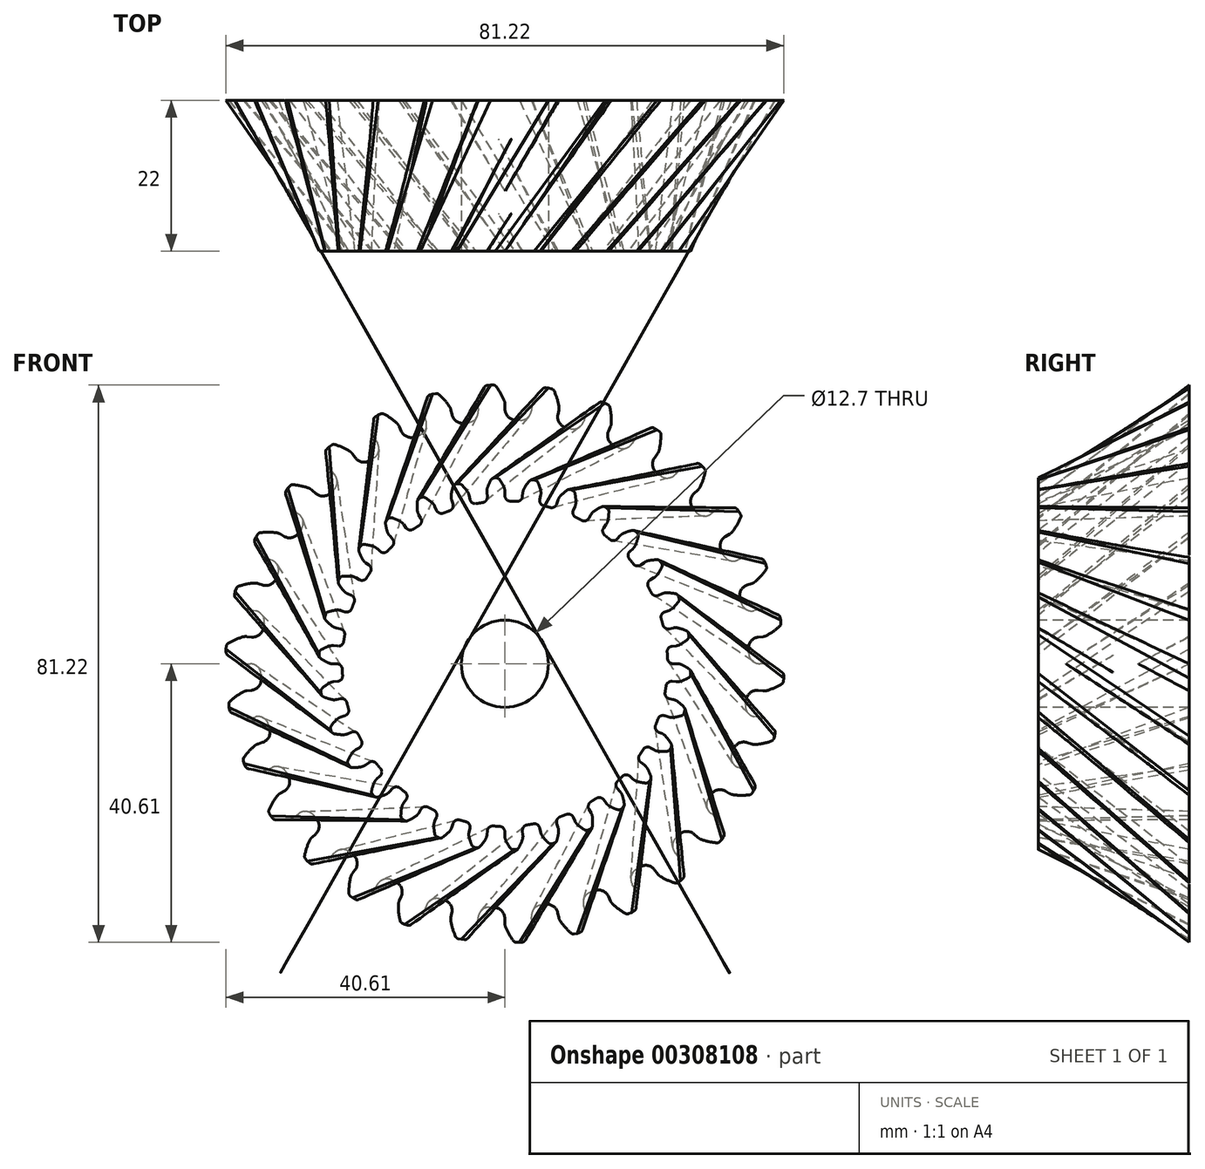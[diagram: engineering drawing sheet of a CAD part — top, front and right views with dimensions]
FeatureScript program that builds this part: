
annotation { "Feature Type Name" : "Feature", "Feature Type Description" : "" }
export const myFeature = defineFeature(function(context is Context, id is Id, definition is map)
    precondition{}
    {
        {
            var Q0;
            Q0=qCreatedBy(makeId("Front.planeOp"),FACE);
            var sketch = newSketch(context, id + "F0", { "sketchPlane" : qUnion([Q0])});
            skArc(sketch, "E0", {"start": v(-5.23, 35.17) * mm, "mid": v(-5.56, 35.12) * mm, "end": v(-5.9, 35.07) * mm});
            skArc(sketch, "E1.trimOffspring", {"start": v(-0.12, 38.41) * mm, "mid": v(-0.63, 39.45) * mm, "end": v(-1.27, 40.41) * mm});
            skLineSegment(sketch, "E2", {"start": v(-1.68, 40.61) * mm, "end": v(-2.13, 40.61) * mm});
            skLineSegment(sketch, "E3", {"start": v(0, 37.8) * mm, "end": v(0, 37.11) * mm});
            skLineSegment(sketch, "E4.MirrorCS", {"start": v(-2.58, 40.57) * mm, "end": v(-2.13, 40.61) * mm});
            skArc(sketch, "E5.MirrorCS", {"start": v(-3.9, 38.22) * mm, "mid": v(-3.5, 39.3) * mm, "end": v(-2.96, 40.32) * mm});
            skLineSegment(sketch, "E6.MirrorCS", {"start": v(-3.96, 37.58) * mm, "end": v(-3.89, 36.9) * mm});
            skPoint(sketch, "E7.visualSharp", {"position": v(-2.82, 40.54) * mm});
            skArc(sketch, "E7.filletArc", {"start": v(-2.58, 40.57) * mm, "mid": v(-2.8, 40.5) * mm, "end": v(-2.96, 40.32) * mm});
            skPoint(sketch, "E8.visualSharp", {"position": v(-1.43, 40.61) * mm});
            skArc(sketch, "E8.filletArc", {"start": v(-1.27, 40.41) * mm, "mid": v(-1.45, 40.56) * mm, "end": v(-1.68, 40.61) * mm});
            skPoint(sketch, "E9.visualSharp", {"position": v(-4, 37.9) * mm});
            skArc(sketch, "E9.filletArc", {"start": v(-3.9, 38.22) * mm, "mid": v(-3.96, 37.9) * mm, "end": v(-3.96, 37.58) * mm});
            skPoint(sketch, "E10.visualSharp", {"position": v(0, 38.1) * mm});
            skArc(sketch, "E10.filletArc", {"start": v(0, 37.8) * mm, "mid": v(-0.02, 38.1) * mm, "end": v(-0.12, 38.41) * mm});
            skPoint(sketch, "E11.visualSharp", {"position": v(0, 35.56) * mm});
            skArc(sketch, "E11.filletArc", {"start": v(0, 37.11) * mm, "mid": v(0.45, 36.02) * mm, "end": v(1.53, 35.53) * mm});
            skPoint(sketch, "E12.visualSharp", {"position": v(-3.73, 35.36) * mm});
            skArc(sketch, "E12.filletArc", {"start": v(-5.23, 35.17) * mm, "mid": v(-4.21, 35.77) * mm, "end": v(-3.89, 36.9) * mm});
            skArc(sketch, "E13.1.0", {"start": v(-12.43, 33.32) * mm, "mid": v(-11.56, 34.11) * mm, "end": v(-11.48, 35.3) * mm});
            skLineSegment(sketch, "E13.1.1", {"start": v(-11.69, 35.94) * mm, "end": v(-11.48, 35.3) * mm});
            skArc(sketch, "E13.1.2", {"start": v(-11.76, 36.57) * mm, "mid": v(-11.75, 36.25) * mm, "end": v(-11.69, 35.94) * mm});
            skArc(sketch, "E13.1.3", {"start": v(-11.76, 36.57) * mm, "mid": v(-11.59, 37.71) * mm, "end": v(-11.28, 38.83) * mm});
            skArc(sketch, "E13.1.4", {"start": v(-10.95, 39.15) * mm, "mid": v(-11.15, 39.02) * mm, "end": v(-11.28, 38.83) * mm});
            skLineSegment(sketch, "E13.1.5", {"start": v(-10.95, 39.15) * mm, "end": v(-10.53, 39.28) * mm});
            skLineSegment(sketch, "E13.1.6", {"start": v(-10.09, 39.38) * mm, "end": v(-10.53, 39.28) * mm});
            skArc(sketch, "E13.1.7", {"start": v(-9.65, 39.26) * mm, "mid": v(-9.85, 39.37) * mm, "end": v(-10.09, 39.38) * mm});
            skArc(sketch, "E13.1.8", {"start": v(-7.85, 36.97) * mm, "mid": v(-7.95, 37.27) * mm, "end": v(-8.1, 37.55) * mm});
            skLineSegment(sketch, "E13.1.9", {"start": v(-7.85, 36.97) * mm, "end": v(-7.7, 36.3) * mm});
            skArc(sketch, "E13.1.10", {"start": v(-7.7, 36.3) * mm, "mid": v(-7.05, 35.32) * mm, "end": v(-5.9, 35.07) * mm});
            skArc(sketch, "E13.1.11", {"start": v(-8.1, 37.55) * mm, "mid": v(-8.82, 38.45) * mm, "end": v(-9.65, 39.26) * mm});
            skArc(sketch, "E13.2.0", {"start": v(-19.09, 30) * mm, "mid": v(-18.4, 30.97) * mm, "end": v(-18.56, 32.14) * mm});
            skLineSegment(sketch, "E13.2.1", {"start": v(-18.9, 32.72) * mm, "end": v(-18.56, 32.14) * mm});
            skArc(sketch, "E13.2.2", {"start": v(-19.1, 33.33) * mm, "mid": v(-19.03, 33.01) * mm, "end": v(-18.9, 32.72) * mm});
            skArc(sketch, "E13.2.3", {"start": v(-19.1, 33.33) * mm, "mid": v(-19.17, 34.48) * mm, "end": v(-19.1, 35.63) * mm});
            skArc(sketch, "E13.2.4", {"start": v(-18.85, 36.01) * mm, "mid": v(-19.02, 35.85) * mm, "end": v(-19.1, 35.63) * mm});
            skLineSegment(sketch, "E13.2.5", {"start": v(-18.85, 36.01) * mm, "end": v(-18.46, 36.24) * mm});
            skLineSegment(sketch, "E13.2.6", {"start": v(-18.05, 36.42) * mm, "end": v(-18.46, 36.24) * mm});
            skArc(sketch, "E13.2.7", {"start": v(-17.6, 36.4) * mm, "mid": v(-17.82, 36.46) * mm, "end": v(-18.05, 36.42) * mm});
            skArc(sketch, "E13.2.8", {"start": v(-15.36, 34.53) * mm, "mid": v(-15.52, 34.8) * mm, "end": v(-15.73, 35.04) * mm});
            skLineSegment(sketch, "E13.2.9", {"start": v(-15.36, 34.53) * mm, "end": v(-15.09, 33.9) * mm});
            skArc(sketch, "E13.2.10", {"start": v(-15.09, 33.9) * mm, "mid": v(-14.24, 33.08) * mm, "end": v(-13.05, 33.08) * mm});
            skArc(sketch, "E13.2.11", {"start": v(-15.73, 35.04) * mm, "mid": v(-16.62, 35.78) * mm, "end": v(-17.6, 36.4) * mm});
            skArc(sketch, "E13.3.0", {"start": v(-24.9, 25.38) * mm, "mid": v(-24.43, 26.46) * mm, "end": v(-24.84, 27.57) * mm});
            skLineSegment(sketch, "E13.3.1", {"start": v(-25.3, 28.08) * mm, "end": v(-24.84, 27.57) * mm});
            skArc(sketch, "E13.3.2", {"start": v(-25.62, 28.63) * mm, "mid": v(-25.48, 28.34) * mm, "end": v(-25.3, 28.08) * mm});
            skArc(sketch, "E13.3.3", {"start": v(-25.62, 28.63) * mm, "mid": v(-25.92, 29.74) * mm, "end": v(-26.1, 30.88) * mm});
            skArc(sketch, "E13.3.4", {"start": v(-25.93, 31.3) * mm, "mid": v(-26.06, 31.11) * mm, "end": v(-26.1, 30.88) * mm});
            skLineSegment(sketch, "E13.3.5", {"start": v(-25.93, 31.3) * mm, "end": v(-25.6, 31.6) * mm});
            skLineSegment(sketch, "E13.3.6", {"start": v(-25.23, 31.87) * mm, "end": v(-25.6, 31.6) * mm});
            skArc(sketch, "E13.3.7", {"start": v(-24.78, 31.95) * mm, "mid": v(-25.02, 31.96) * mm, "end": v(-25.23, 31.87) * mm});
            skArc(sketch, "E13.3.8", {"start": v(-22.2, 30.58) * mm, "mid": v(-22.42, 30.82) * mm, "end": v(-22.67, 31) * mm});
            skLineSegment(sketch, "E13.3.9", {"start": v(-22.2, 30.58) * mm, "end": v(-21.8, 30.03) * mm});
            skArc(sketch, "E13.3.10", {"start": v(-21.8, 30.03) * mm, "mid": v(-20.8, 29.4) * mm, "end": v(-19.65, 29.64) * mm});
            skArc(sketch, "E13.3.11", {"start": v(-22.67, 31) * mm, "mid": v(-23.7, 31.54) * mm, "end": v(-24.78, 31.95) * mm});
            skArc(sketch, "E13.4.0", {"start": v(-29.64, 19.65) * mm, "mid": v(-29.4, 20.8) * mm, "end": v(-30.03, 21.8) * mm});
            skLineSegment(sketch, "E13.4.1", {"start": v(-30.58, 22.2) * mm, "end": v(-30.03, 21.8) * mm});
            skArc(sketch, "E13.4.2", {"start": v(-31, 22.67) * mm, "mid": v(-30.82, 22.42) * mm, "end": v(-30.58, 22.2) * mm});
            skArc(sketch, "E13.4.3", {"start": v(-31, 22.67) * mm, "mid": v(-31.54, 23.7) * mm, "end": v(-31.95, 24.78) * mm});
            skArc(sketch, "E13.4.4", {"start": v(-31.87, 25.23) * mm, "mid": v(-31.96, 25.02) * mm, "end": v(-31.95, 24.78) * mm});
            skLineSegment(sketch, "E13.4.5", {"start": v(-31.87, 25.23) * mm, "end": v(-31.6, 25.6) * mm});
            skLineSegment(sketch, "E13.4.6", {"start": v(-31.3, 25.93) * mm, "end": v(-31.6, 25.6) * mm});
            skArc(sketch, "E13.4.7", {"start": v(-30.88, 26.1) * mm, "mid": v(-31.11, 26.06) * mm, "end": v(-31.3, 25.93) * mm});
            skArc(sketch, "E13.4.8", {"start": v(-28.08, 25.3) * mm, "mid": v(-28.34, 25.48) * mm, "end": v(-28.63, 25.62) * mm});
            skLineSegment(sketch, "E13.4.9", {"start": v(-28.08, 25.3) * mm, "end": v(-27.57, 24.84) * mm});
            skArc(sketch, "E13.4.10", {"start": v(-27.57, 24.84) * mm, "mid": v(-26.46, 24.43) * mm, "end": v(-25.38, 24.9) * mm});
            skArc(sketch, "E13.4.11", {"start": v(-28.63, 25.62) * mm, "mid": v(-29.74, 25.92) * mm, "end": v(-30.88, 26.1) * mm});
            skArc(sketch, "E13.5.0", {"start": v(-33.08, 13.05) * mm, "mid": v(-33.08, 14.24) * mm, "end": v(-33.9, 15.09) * mm});
            skLineSegment(sketch, "E13.5.1", {"start": v(-34.53, 15.36) * mm, "end": v(-33.9, 15.09) * mm});
            skArc(sketch, "E13.5.2", {"start": v(-35.04, 15.73) * mm, "mid": v(-34.8, 15.52) * mm, "end": v(-34.53, 15.36) * mm});
            skArc(sketch, "E13.5.3", {"start": v(-35.04, 15.73) * mm, "mid": v(-35.78, 16.62) * mm, "end": v(-36.4, 17.6) * mm});
            skArc(sketch, "E13.5.4", {"start": v(-36.42, 18.05) * mm, "mid": v(-36.46, 17.82) * mm, "end": v(-36.4, 17.6) * mm});
            skLineSegment(sketch, "E13.5.5", {"start": v(-36.42, 18.05) * mm, "end": v(-36.24, 18.46) * mm});
            skLineSegment(sketch, "E13.5.6", {"start": v(-36.01, 18.85) * mm, "end": v(-36.24, 18.46) * mm});
            skArc(sketch, "E13.5.7", {"start": v(-35.63, 19.1) * mm, "mid": v(-35.85, 19.02) * mm, "end": v(-36.01, 18.85) * mm});
            skArc(sketch, "E13.5.8", {"start": v(-32.72, 18.9) * mm, "mid": v(-33.01, 19.03) * mm, "end": v(-33.33, 19.1) * mm});
            skLineSegment(sketch, "E13.5.9", {"start": v(-32.72, 18.9) * mm, "end": v(-32.14, 18.56) * mm});
            skArc(sketch, "E13.5.10", {"start": v(-32.14, 18.56) * mm, "mid": v(-30.97, 18.4) * mm, "end": v(-30, 19.09) * mm});
            skArc(sketch, "E13.5.11", {"start": v(-33.33, 19.1) * mm, "mid": v(-34.48, 19.17) * mm, "end": v(-35.63, 19.1) * mm});
            skArc(sketch, "E13.6.0", {"start": v(-35.07, 5.9) * mm, "mid": v(-35.32, 7.05) * mm, "end": v(-36.3, 7.7) * mm});
            skLineSegment(sketch, "E13.6.1", {"start": v(-36.97, 7.85) * mm, "end": v(-36.3, 7.7) * mm});
            skArc(sketch, "E13.6.2", {"start": v(-37.55, 8.1) * mm, "mid": v(-37.27, 7.95) * mm, "end": v(-36.97, 7.85) * mm});
            skArc(sketch, "E13.6.3", {"start": v(-37.55, 8.1) * mm, "mid": v(-38.45, 8.82) * mm, "end": v(-39.26, 9.65) * mm});
            skArc(sketch, "E13.6.4", {"start": v(-39.38, 10.09) * mm, "mid": v(-39.37, 9.85) * mm, "end": v(-39.26, 9.65) * mm});
            skLineSegment(sketch, "E13.6.5", {"start": v(-39.38, 10.09) * mm, "end": v(-39.28, 10.53) * mm});
            skLineSegment(sketch, "E13.6.6", {"start": v(-39.15, 10.95) * mm, "end": v(-39.28, 10.53) * mm});
            skArc(sketch, "E13.6.7", {"start": v(-38.83, 11.28) * mm, "mid": v(-39.02, 11.15) * mm, "end": v(-39.15, 10.95) * mm});
            skArc(sketch, "E13.6.8", {"start": v(-35.94, 11.69) * mm, "mid": v(-36.25, 11.75) * mm, "end": v(-36.57, 11.76) * mm});
            skLineSegment(sketch, "E13.6.9", {"start": v(-35.94, 11.69) * mm, "end": v(-35.3, 11.48) * mm});
            skArc(sketch, "E13.6.10", {"start": v(-35.3, 11.48) * mm, "mid": v(-34.11, 11.56) * mm, "end": v(-33.32, 12.43) * mm});
            skArc(sketch, "E13.6.11", {"start": v(-36.57, 11.76) * mm, "mid": v(-37.71, 11.59) * mm, "end": v(-38.83, 11.28) * mm});
            skArc(sketch, "E13.7.0", {"start": v(-35.53, -1.53) * mm, "mid": v(-36.02, -0.45) * mm, "end": v(-37.11, 0) * mm});
            skLineSegment(sketch, "E13.7.1", {"start": v(-37.8, 0) * mm, "end": v(-37.11, 0) * mm});
            skArc(sketch, "E13.7.2", {"start": v(-38.41, 0.12) * mm, "mid": v(-38.1, 0.02) * mm, "end": v(-37.8, 0) * mm});
            skArc(sketch, "E13.7.3", {"start": v(-38.41, 0.12) * mm, "mid": v(-39.45, 0.63) * mm, "end": v(-40.41, 1.27) * mm});
            skArc(sketch, "E13.7.4", {"start": v(-40.61, 1.68) * mm, "mid": v(-40.56, 1.45) * mm, "end": v(-40.41, 1.27) * mm});
            skLineSegment(sketch, "E13.7.5", {"start": v(-40.61, 1.68) * mm, "end": v(-40.61, 2.13) * mm});
            skLineSegment(sketch, "E13.7.6", {"start": v(-40.57, 2.58) * mm, "end": v(-40.61, 2.13) * mm});
            skArc(sketch, "E13.7.7", {"start": v(-40.32, 2.96) * mm, "mid": v(-40.5, 2.8) * mm, "end": v(-40.57, 2.58) * mm});
            skArc(sketch, "E13.7.8", {"start": v(-37.58, 3.96) * mm, "mid": v(-37.9, 3.96) * mm, "end": v(-38.22, 3.9) * mm});
            skLineSegment(sketch, "E13.7.9", {"start": v(-37.58, 3.96) * mm, "end": v(-36.9, 3.89) * mm});
            skArc(sketch, "E13.7.10", {"start": v(-36.9, 3.89) * mm, "mid": v(-35.77, 4.21) * mm, "end": v(-35.17, 5.23) * mm});
            skArc(sketch, "E13.7.11", {"start": v(-38.22, 3.9) * mm, "mid": v(-39.3, 3.5) * mm, "end": v(-40.32, 2.96) * mm});
            skArc(sketch, "E13.8.0", {"start": v(-34.43, -8.88) * mm, "mid": v(-35.13, -7.93) * mm, "end": v(-36.3, -7.72) * mm});
            skLineSegment(sketch, "E13.8.1", {"start": v(-36.96, -7.87) * mm, "end": v(-36.3, -7.72) * mm});
            skArc(sketch, "E13.8.2", {"start": v(-37.6, -7.87) * mm, "mid": v(-37.28, -7.9) * mm, "end": v(-36.96, -7.87) * mm});
            skArc(sketch, "E13.8.3", {"start": v(-37.6, -7.87) * mm, "mid": v(-38.72, -7.58) * mm, "end": v(-39.8, -7.16) * mm});
            skArc(sketch, "E13.8.4", {"start": v(-40.08, -6.8) * mm, "mid": v(-39.98, -7.01) * mm, "end": v(-39.8, -7.16) * mm});
            skLineSegment(sketch, "E13.8.5", {"start": v(-40.08, -6.8) * mm, "end": v(-40.17, -6.36) * mm});
            skLineSegment(sketch, "E13.8.6", {"start": v(-40.22, -5.92) * mm, "end": v(-40.17, -6.36) * mm});
            skArc(sketch, "E13.8.7", {"start": v(-40.06, -5.5) * mm, "mid": v(-40.19, -5.68) * mm, "end": v(-40.22, -5.92) * mm});
            skArc(sketch, "E13.8.8", {"start": v(-37.59, -3.94) * mm, "mid": v(-37.9, -4) * mm, "end": v(-38.2, -4.13) * mm});
            skLineSegment(sketch, "E13.8.9", {"start": v(-37.59, -3.94) * mm, "end": v(-36.91, -3.87) * mm});
            skArc(sketch, "E13.8.10", {"start": v(-36.91, -3.87) * mm, "mid": v(-35.86, -3.32) * mm, "end": v(-35.5, -2.2) * mm});
            skArc(sketch, "E13.8.11", {"start": v(-38.2, -4.13) * mm, "mid": v(-39.17, -4.75) * mm, "end": v(-40.06, -5.5) * mm});
            skArc(sketch, "E13.9.0", {"start": v(-31.83, -15.85) * mm, "mid": v(-32.72, -15.06) * mm, "end": v(-33.9, -15.1) * mm});
            skLineSegment(sketch, "E13.9.1", {"start": v(-34.52, -15.38) * mm, "end": v(-33.9, -15.1) * mm});
            skArc(sketch, "E13.9.2", {"start": v(-35.14, -15.52) * mm, "mid": v(-34.82, -15.48) * mm, "end": v(-34.52, -15.38) * mm});
            skArc(sketch, "E13.9.3", {"start": v(-35.14, -15.52) * mm, "mid": v(-36.3, -15.46) * mm, "end": v(-37.44, -15.27) * mm});
            skArc(sketch, "E13.9.4", {"start": v(-37.79, -14.99) * mm, "mid": v(-37.65, -15.17) * mm, "end": v(-37.44, -15.27) * mm});
            skLineSegment(sketch, "E13.9.5", {"start": v(-37.79, -14.99) * mm, "end": v(-37.97, -14.58) * mm});
            skLineSegment(sketch, "E13.9.6", {"start": v(-38.1, -14.15) * mm, "end": v(-37.97, -14.58) * mm});
            skArc(sketch, "E13.9.7", {"start": v(-38.04, -13.7) * mm, "mid": v(-38.13, -13.92) * mm, "end": v(-38.1, -14.15) * mm});
            skArc(sketch, "E13.9.8", {"start": v(-35.94, -11.67) * mm, "mid": v(-36.24, -11.8) * mm, "end": v(-36.5, -11.98) * mm});
            skLineSegment(sketch, "E13.9.9", {"start": v(-35.94, -11.67) * mm, "end": v(-35.3, -11.46) * mm});
            skArc(sketch, "E13.9.10", {"start": v(-35.3, -11.46) * mm, "mid": v(-34.4, -10.7) * mm, "end": v(-34.26, -9.53) * mm});
            skArc(sketch, "E13.9.11", {"start": v(-36.5, -11.98) * mm, "mid": v(-37.32, -12.8) * mm, "end": v(-38.04, -13.7) * mm});
            skArc(sketch, "E13.10.0", {"start": v(-27.84, -22.12) * mm, "mid": v(-28.87, -21.53) * mm, "end": v(-30.02, -21.82) * mm});
            skLineSegment(sketch, "E13.10.1", {"start": v(-30.57, -22.22) * mm, "end": v(-30.02, -21.82) * mm});
            skArc(sketch, "E13.10.2", {"start": v(-31.15, -22.48) * mm, "mid": v(-30.84, -22.38) * mm, "end": v(-30.57, -22.22) * mm});
            skArc(sketch, "E13.10.3", {"start": v(-31.15, -22.48) * mm, "mid": v(-32.29, -22.67) * mm, "end": v(-33.44, -22.72) * mm});
            skArc(sketch, "E13.10.4", {"start": v(-33.85, -22.51) * mm, "mid": v(-33.67, -22.67) * mm, "end": v(-33.44, -22.72) * mm});
            skLineSegment(sketch, "E13.10.5", {"start": v(-33.85, -22.51) * mm, "end": v(-34.1, -22.15) * mm});
            skLineSegment(sketch, "E13.10.6", {"start": v(-34.33, -21.76) * mm, "end": v(-34.1, -22.15) * mm});
            skArc(sketch, "E13.10.7", {"start": v(-34.36, -21.3) * mm, "mid": v(-34.4, -21.54) * mm, "end": v(-34.33, -21.76) * mm});
            skArc(sketch, "E13.10.8", {"start": v(-32.73, -18.89) * mm, "mid": v(-33, -19.07) * mm, "end": v(-33.2, -19.3) * mm});
            skLineSegment(sketch, "E13.10.9", {"start": v(-32.73, -18.89) * mm, "end": v(-32.15, -18.55) * mm});
            skArc(sketch, "E13.10.10", {"start": v(-32.15, -18.55) * mm, "mid": v(-31.41, -17.62) * mm, "end": v(-31.53, -16.44) * mm});
            skArc(sketch, "E13.10.11", {"start": v(-33.2, -19.3) * mm, "mid": v(-33.85, -20.27) * mm, "end": v(-34.36, -21.3) * mm});
            skArc(sketch, "E13.11.0", {"start": v(-22.64, -27.42) * mm, "mid": v(-23.76, -27.07) * mm, "end": v(-24.83, -27.59) * mm});
            skLineSegment(sketch, "E13.11.1", {"start": v(-25.28, -28.1) * mm, "end": v(-24.83, -27.59) * mm});
            skArc(sketch, "E13.11.2", {"start": v(-25.8, -28.47) * mm, "mid": v(-25.52, -28.3) * mm, "end": v(-25.28, -28.1) * mm});
            skArc(sketch, "E13.11.3", {"start": v(-25.8, -28.47) * mm, "mid": v(-26.87, -28.9) * mm, "end": v(-27.99, -29.18) * mm});
            skArc(sketch, "E13.11.4", {"start": v(-28.42, -29.06) * mm, "mid": v(-28.22, -29.17) * mm, "end": v(-27.99, -29.18) * mm});
            skLineSegment(sketch, "E13.11.5", {"start": v(-28.42, -29.06) * mm, "end": v(-28.76, -28.76) * mm});
            skLineSegment(sketch, "E13.11.6", {"start": v(-29.06, -28.42) * mm, "end": v(-28.76, -28.76) * mm});
            skArc(sketch, "E13.11.7", {"start": v(-29.18, -27.99) * mm, "mid": v(-29.17, -28.22) * mm, "end": v(-29.06, -28.42) * mm});
            skArc(sketch, "E13.11.8", {"start": v(-28.1, -25.28) * mm, "mid": v(-28.3, -25.52) * mm, "end": v(-28.47, -25.8) * mm});
            skLineSegment(sketch, "E13.11.9", {"start": v(-28.1, -25.28) * mm, "end": v(-27.59, -24.83) * mm});
            skArc(sketch, "E13.11.10", {"start": v(-27.59, -24.83) * mm, "mid": v(-27.07, -23.76) * mm, "end": v(-27.42, -22.64) * mm});
            skArc(sketch, "E13.11.11", {"start": v(-28.47, -25.8) * mm, "mid": v(-28.9, -26.87) * mm, "end": v(-29.18, -27.99) * mm});
            skArc(sketch, "E13.12.0", {"start": v(-16.44, -31.53) * mm, "mid": v(-17.62, -31.41) * mm, "end": v(-18.55, -32.15) * mm});
            skLineSegment(sketch, "E13.12.1", {"start": v(-18.89, -32.73) * mm, "end": v(-18.55, -32.15) * mm});
            skArc(sketch, "E13.12.2", {"start": v(-19.3, -33.2) * mm, "mid": v(-19.07, -33) * mm, "end": v(-18.89, -32.73) * mm});
            skArc(sketch, "E13.12.3", {"start": v(-19.3, -33.2) * mm, "mid": v(-20.27, -33.85) * mm, "end": v(-21.3, -34.36) * mm});
            skArc(sketch, "E13.12.4", {"start": v(-21.76, -34.33) * mm, "mid": v(-21.54, -34.4) * mm, "end": v(-21.3, -34.36) * mm});
            skLineSegment(sketch, "E13.12.5", {"start": v(-21.76, -34.33) * mm, "end": v(-22.15, -34.1) * mm});
            skLineSegment(sketch, "E13.12.6", {"start": v(-22.51, -33.85) * mm, "end": v(-22.15, -34.1) * mm});
            skArc(sketch, "E13.12.7", {"start": v(-22.72, -33.44) * mm, "mid": v(-22.67, -33.67) * mm, "end": v(-22.51, -33.85) * mm});
            skArc(sketch, "E13.12.8", {"start": v(-22.22, -30.57) * mm, "mid": v(-22.38, -30.84) * mm, "end": v(-22.48, -31.15) * mm});
            skLineSegment(sketch, "E13.12.9", {"start": v(-22.22, -30.57) * mm, "end": v(-21.82, -30.02) * mm});
            skArc(sketch, "E13.12.10", {"start": v(-21.82, -30.02) * mm, "mid": v(-21.53, -28.87) * mm, "end": v(-22.12, -27.84) * mm});
            skArc(sketch, "E13.12.11", {"start": v(-22.48, -31.15) * mm, "mid": v(-22.67, -32.29) * mm, "end": v(-22.72, -33.44) * mm});
            skArc(sketch, "E13.13.0", {"start": v(-9.53, -34.26) * mm, "mid": v(-10.7, -34.4) * mm, "end": v(-11.46, -35.3) * mm});
            skLineSegment(sketch, "E13.13.1", {"start": v(-11.67, -35.94) * mm, "end": v(-11.46, -35.3) * mm});
            skArc(sketch, "E13.13.2", {"start": v(-11.98, -36.5) * mm, "mid": v(-11.8, -36.24) * mm, "end": v(-11.67, -35.94) * mm});
            skArc(sketch, "E13.13.3", {"start": v(-11.98, -36.5) * mm, "mid": v(-12.8, -37.32) * mm, "end": v(-13.7, -38.04) * mm});
            skArc(sketch, "E13.13.4", {"start": v(-14.15, -38.1) * mm, "mid": v(-13.92, -38.13) * mm, "end": v(-13.7, -38.04) * mm});
            skLineSegment(sketch, "E13.13.5", {"start": v(-14.15, -38.1) * mm, "end": v(-14.58, -37.97) * mm});
            skLineSegment(sketch, "E13.13.6", {"start": v(-14.99, -37.79) * mm, "end": v(-14.58, -37.97) * mm});
            skArc(sketch, "E13.13.7", {"start": v(-15.27, -37.44) * mm, "mid": v(-15.17, -37.65) * mm, "end": v(-14.99, -37.79) * mm});
            skArc(sketch, "E13.13.8", {"start": v(-15.38, -34.52) * mm, "mid": v(-15.48, -34.82) * mm, "end": v(-15.52, -35.14) * mm});
            skLineSegment(sketch, "E13.13.9", {"start": v(-15.38, -34.52) * mm, "end": v(-15.1, -33.9) * mm});
            skArc(sketch, "E13.13.10", {"start": v(-15.1, -33.9) * mm, "mid": v(-15.06, -32.72) * mm, "end": v(-15.85, -31.83) * mm});
            skArc(sketch, "E13.13.11", {"start": v(-15.52, -35.14) * mm, "mid": v(-15.46, -36.3) * mm, "end": v(-15.27, -37.44) * mm});
            skArc(sketch, "E13.14.0", {"start": v(-2.2, -35.5) * mm, "mid": v(-3.32, -35.86) * mm, "end": v(-3.87, -36.91) * mm});
            skLineSegment(sketch, "E13.14.1", {"start": v(-3.94, -37.59) * mm, "end": v(-3.87, -36.91) * mm});
            skArc(sketch, "E13.14.2", {"start": v(-4.13, -38.2) * mm, "mid": v(-4, -37.9) * mm, "end": v(-3.94, -37.59) * mm});
            skArc(sketch, "E13.14.3", {"start": v(-4.13, -38.2) * mm, "mid": v(-4.75, -39.17) * mm, "end": v(-5.5, -40.06) * mm});
            skArc(sketch, "E13.14.4", {"start": v(-5.92, -40.22) * mm, "mid": v(-5.68, -40.19) * mm, "end": v(-5.5, -40.06) * mm});
            skLineSegment(sketch, "E13.14.5", {"start": v(-5.92, -40.22) * mm, "end": v(-6.36, -40.17) * mm});
            skLineSegment(sketch, "E13.14.6", {"start": v(-6.8, -40.08) * mm, "end": v(-6.36, -40.17) * mm});
            skArc(sketch, "E13.14.7", {"start": v(-7.16, -39.8) * mm, "mid": v(-7.01, -39.98) * mm, "end": v(-6.8, -40.08) * mm});
            skArc(sketch, "E13.14.8", {"start": v(-7.87, -36.96) * mm, "mid": v(-7.9, -37.28) * mm, "end": v(-7.87, -37.6) * mm});
            skLineSegment(sketch, "E13.14.9", {"start": v(-7.87, -36.96) * mm, "end": v(-7.72, -36.3) * mm});
            skArc(sketch, "E13.14.10", {"start": v(-7.72, -36.3) * mm, "mid": v(-7.93, -35.13) * mm, "end": v(-8.88, -34.43) * mm});
            skArc(sketch, "E13.14.11", {"start": v(-7.87, -37.6) * mm, "mid": v(-7.58, -38.72) * mm, "end": v(-7.16, -39.8) * mm});
            skArc(sketch, "E13.15.0", {"start": v(5.23, -35.17) * mm, "mid": v(4.21, -35.77) * mm, "end": v(3.89, -36.9) * mm});
            skLineSegment(sketch, "E13.15.1", {"start": v(3.96, -37.58) * mm, "end": v(3.89, -36.9) * mm});
            skArc(sketch, "E13.15.2", {"start": v(3.9, -38.22) * mm, "mid": v(3.96, -37.9) * mm, "end": v(3.96, -37.58) * mm});
            skArc(sketch, "E13.15.3", {"start": v(3.9, -38.22) * mm, "mid": v(3.5, -39.3) * mm, "end": v(2.96, -40.32) * mm});
            skArc(sketch, "E13.15.4", {"start": v(2.58, -40.57) * mm, "mid": v(2.8, -40.5) * mm, "end": v(2.96, -40.32) * mm});
            skLineSegment(sketch, "E13.15.5", {"start": v(2.58, -40.57) * mm, "end": v(2.13, -40.61) * mm});
            skLineSegment(sketch, "E13.15.6", {"start": v(1.68, -40.61) * mm, "end": v(2.13, -40.61) * mm});
            skArc(sketch, "E13.15.7", {"start": v(1.27, -40.41) * mm, "mid": v(1.45, -40.56) * mm, "end": v(1.68, -40.61) * mm});
            skArc(sketch, "E13.15.8", {"start": v(0, -37.8) * mm, "mid": v(0.02, -38.1) * mm, "end": v(0.12, -38.41) * mm});
            skLineSegment(sketch, "E13.15.9", {"start": v(0, -37.8) * mm, "end": v(0, -37.11) * mm});
            skArc(sketch, "E13.15.10", {"start": v(0, -37.11) * mm, "mid": v(-0.45, -36.02) * mm, "end": v(-1.53, -35.53) * mm});
            skArc(sketch, "E13.15.11", {"start": v(0.12, -38.41) * mm, "mid": v(0.63, -39.45) * mm, "end": v(1.27, -40.41) * mm});
            skArc(sketch, "E13.16.0", {"start": v(12.43, -33.32) * mm, "mid": v(11.56, -34.11) * mm, "end": v(11.48, -35.3) * mm});
            skLineSegment(sketch, "E13.16.1", {"start": v(11.69, -35.94) * mm, "end": v(11.48, -35.3) * mm});
            skArc(sketch, "E13.16.2", {"start": v(11.76, -36.57) * mm, "mid": v(11.75, -36.25) * mm, "end": v(11.69, -35.94) * mm});
            skArc(sketch, "E13.16.3", {"start": v(11.76, -36.57) * mm, "mid": v(11.59, -37.71) * mm, "end": v(11.28, -38.83) * mm});
            skArc(sketch, "E13.16.4", {"start": v(10.95, -39.15) * mm, "mid": v(11.15, -39.02) * mm, "end": v(11.28, -38.83) * mm});
            skLineSegment(sketch, "E13.16.5", {"start": v(10.95, -39.15) * mm, "end": v(10.53, -39.28) * mm});
            skLineSegment(sketch, "E13.16.6", {"start": v(10.09, -39.38) * mm, "end": v(10.53, -39.28) * mm});
            skArc(sketch, "E13.16.7", {"start": v(9.65, -39.26) * mm, "mid": v(9.85, -39.37) * mm, "end": v(10.09, -39.38) * mm});
            skArc(sketch, "E13.16.8", {"start": v(7.85, -36.97) * mm, "mid": v(7.95, -37.27) * mm, "end": v(8.1, -37.55) * mm});
            skLineSegment(sketch, "E13.16.9", {"start": v(7.85, -36.97) * mm, "end": v(7.7, -36.3) * mm});
            skArc(sketch, "E13.16.10", {"start": v(7.7, -36.3) * mm, "mid": v(7.05, -35.32) * mm, "end": v(5.9, -35.07) * mm});
            skArc(sketch, "E13.16.11", {"start": v(8.1, -37.55) * mm, "mid": v(8.82, -38.45) * mm, "end": v(9.65, -39.26) * mm});
            skArc(sketch, "E13.17.0", {"start": v(19.09, -30) * mm, "mid": v(18.4, -30.97) * mm, "end": v(18.56, -32.14) * mm});
            skLineSegment(sketch, "E13.17.1", {"start": v(18.9, -32.72) * mm, "end": v(18.56, -32.14) * mm});
            skArc(sketch, "E13.17.2", {"start": v(19.1, -33.33) * mm, "mid": v(19.03, -33.01) * mm, "end": v(18.9, -32.72) * mm});
            skArc(sketch, "E13.17.3", {"start": v(19.1, -33.33) * mm, "mid": v(19.17, -34.48) * mm, "end": v(19.1, -35.63) * mm});
            skArc(sketch, "E13.17.4", {"start": v(18.85, -36.01) * mm, "mid": v(19.02, -35.85) * mm, "end": v(19.1, -35.63) * mm});
            skLineSegment(sketch, "E13.17.5", {"start": v(18.85, -36.01) * mm, "end": v(18.46, -36.24) * mm});
            skLineSegment(sketch, "E13.17.6", {"start": v(18.05, -36.42) * mm, "end": v(18.46, -36.24) * mm});
            skArc(sketch, "E13.17.7", {"start": v(17.6, -36.4) * mm, "mid": v(17.82, -36.46) * mm, "end": v(18.05, -36.42) * mm});
            skArc(sketch, "E13.17.8", {"start": v(15.36, -34.53) * mm, "mid": v(15.52, -34.8) * mm, "end": v(15.73, -35.04) * mm});
            skLineSegment(sketch, "E13.17.9", {"start": v(15.36, -34.53) * mm, "end": v(15.09, -33.9) * mm});
            skArc(sketch, "E13.17.10", {"start": v(15.09, -33.9) * mm, "mid": v(14.24, -33.08) * mm, "end": v(13.05, -33.08) * mm});
            skArc(sketch, "E13.17.11", {"start": v(15.73, -35.04) * mm, "mid": v(16.62, -35.78) * mm, "end": v(17.6, -36.4) * mm});
            skArc(sketch, "E13.18.0", {"start": v(24.9, -25.38) * mm, "mid": v(24.43, -26.46) * mm, "end": v(24.84, -27.57) * mm});
            skLineSegment(sketch, "E13.18.1", {"start": v(25.3, -28.08) * mm, "end": v(24.84, -27.57) * mm});
            skArc(sketch, "E13.18.2", {"start": v(25.62, -28.63) * mm, "mid": v(25.48, -28.34) * mm, "end": v(25.3, -28.08) * mm});
            skArc(sketch, "E13.18.3", {"start": v(25.62, -28.63) * mm, "mid": v(25.92, -29.74) * mm, "end": v(26.1, -30.88) * mm});
            skArc(sketch, "E13.18.4", {"start": v(25.93, -31.3) * mm, "mid": v(26.06, -31.11) * mm, "end": v(26.1, -30.88) * mm});
            skLineSegment(sketch, "E13.18.5", {"start": v(25.93, -31.3) * mm, "end": v(25.6, -31.6) * mm});
            skLineSegment(sketch, "E13.18.6", {"start": v(25.23, -31.87) * mm, "end": v(25.6, -31.6) * mm});
            skArc(sketch, "E13.18.7", {"start": v(24.78, -31.95) * mm, "mid": v(25.02, -31.96) * mm, "end": v(25.23, -31.87) * mm});
            skArc(sketch, "E13.18.8", {"start": v(22.2, -30.58) * mm, "mid": v(22.42, -30.82) * mm, "end": v(22.67, -31) * mm});
            skLineSegment(sketch, "E13.18.9", {"start": v(22.2, -30.58) * mm, "end": v(21.8, -30.03) * mm});
            skArc(sketch, "E13.18.10", {"start": v(21.8, -30.03) * mm, "mid": v(20.8, -29.4) * mm, "end": v(19.65, -29.64) * mm});
            skArc(sketch, "E13.18.11", {"start": v(22.67, -31) * mm, "mid": v(23.7, -31.54) * mm, "end": v(24.78, -31.95) * mm});
            skArc(sketch, "E13.19.0", {"start": v(29.64, -19.65) * mm, "mid": v(29.4, -20.8) * mm, "end": v(30.03, -21.8) * mm});
            skLineSegment(sketch, "E13.19.1", {"start": v(30.58, -22.2) * mm, "end": v(30.03, -21.8) * mm});
            skArc(sketch, "E13.19.2", {"start": v(31, -22.67) * mm, "mid": v(30.82, -22.42) * mm, "end": v(30.58, -22.2) * mm});
            skArc(sketch, "E13.19.3", {"start": v(31, -22.67) * mm, "mid": v(31.54, -23.7) * mm, "end": v(31.95, -24.78) * mm});
            skArc(sketch, "E13.19.4", {"start": v(31.87, -25.23) * mm, "mid": v(31.96, -25.02) * mm, "end": v(31.95, -24.78) * mm});
            skLineSegment(sketch, "E13.19.5", {"start": v(31.87, -25.23) * mm, "end": v(31.6, -25.6) * mm});
            skLineSegment(sketch, "E13.19.6", {"start": v(31.3, -25.93) * mm, "end": v(31.6, -25.6) * mm});
            skArc(sketch, "E13.19.7", {"start": v(30.88, -26.1) * mm, "mid": v(31.11, -26.06) * mm, "end": v(31.3, -25.93) * mm});
            skArc(sketch, "E13.19.8", {"start": v(28.08, -25.3) * mm, "mid": v(28.34, -25.48) * mm, "end": v(28.63, -25.62) * mm});
            skLineSegment(sketch, "E13.19.9", {"start": v(28.08, -25.3) * mm, "end": v(27.57, -24.84) * mm});
            skArc(sketch, "E13.19.10", {"start": v(27.57, -24.84) * mm, "mid": v(26.46, -24.43) * mm, "end": v(25.38, -24.9) * mm});
            skArc(sketch, "E13.19.11", {"start": v(28.63, -25.62) * mm, "mid": v(29.74, -25.92) * mm, "end": v(30.88, -26.1) * mm});
            skArc(sketch, "E13.20.0", {"start": v(33.08, -13.05) * mm, "mid": v(33.08, -14.24) * mm, "end": v(33.9, -15.09) * mm});
            skLineSegment(sketch, "E13.20.1", {"start": v(34.53, -15.36) * mm, "end": v(33.9, -15.09) * mm});
            skArc(sketch, "E13.20.2", {"start": v(35.04, -15.73) * mm, "mid": v(34.8, -15.52) * mm, "end": v(34.53, -15.36) * mm});
            skArc(sketch, "E13.20.3", {"start": v(35.04, -15.73) * mm, "mid": v(35.78, -16.62) * mm, "end": v(36.4, -17.6) * mm});
            skArc(sketch, "E13.20.4", {"start": v(36.42, -18.05) * mm, "mid": v(36.46, -17.82) * mm, "end": v(36.4, -17.6) * mm});
            skLineSegment(sketch, "E13.20.5", {"start": v(36.42, -18.05) * mm, "end": v(36.24, -18.46) * mm});
            skLineSegment(sketch, "E13.20.6", {"start": v(36.01, -18.85) * mm, "end": v(36.24, -18.46) * mm});
            skArc(sketch, "E13.20.7", {"start": v(35.63, -19.1) * mm, "mid": v(35.85, -19.02) * mm, "end": v(36.01, -18.85) * mm});
            skArc(sketch, "E13.20.8", {"start": v(32.72, -18.9) * mm, "mid": v(33.01, -19.03) * mm, "end": v(33.33, -19.1) * mm});
            skLineSegment(sketch, "E13.20.9", {"start": v(32.72, -18.9) * mm, "end": v(32.14, -18.56) * mm});
            skArc(sketch, "E13.20.10", {"start": v(32.14, -18.56) * mm, "mid": v(30.97, -18.4) * mm, "end": v(30, -19.09) * mm});
            skArc(sketch, "E13.20.11", {"start": v(33.33, -19.1) * mm, "mid": v(34.48, -19.17) * mm, "end": v(35.63, -19.1) * mm});
            skArc(sketch, "E13.21.0", {"start": v(35.07, -5.9) * mm, "mid": v(35.32, -7.05) * mm, "end": v(36.3, -7.7) * mm});
            skLineSegment(sketch, "E13.21.1", {"start": v(36.97, -7.85) * mm, "end": v(36.3, -7.7) * mm});
            skArc(sketch, "E13.21.2", {"start": v(37.55, -8.1) * mm, "mid": v(37.27, -7.95) * mm, "end": v(36.97, -7.85) * mm});
            skArc(sketch, "E13.21.3", {"start": v(37.55, -8.1) * mm, "mid": v(38.45, -8.82) * mm, "end": v(39.26, -9.65) * mm});
            skArc(sketch, "E13.21.4", {"start": v(39.38, -10.09) * mm, "mid": v(39.37, -9.85) * mm, "end": v(39.26, -9.65) * mm});
            skLineSegment(sketch, "E13.21.5", {"start": v(39.38, -10.09) * mm, "end": v(39.28, -10.53) * mm});
            skLineSegment(sketch, "E13.21.6", {"start": v(39.15, -10.95) * mm, "end": v(39.28, -10.53) * mm});
            skArc(sketch, "E13.21.7", {"start": v(38.83, -11.28) * mm, "mid": v(39.02, -11.15) * mm, "end": v(39.15, -10.95) * mm});
            skArc(sketch, "E13.21.8", {"start": v(35.94, -11.69) * mm, "mid": v(36.25, -11.75) * mm, "end": v(36.57, -11.76) * mm});
            skLineSegment(sketch, "E13.21.9", {"start": v(35.94, -11.69) * mm, "end": v(35.3, -11.48) * mm});
            skArc(sketch, "E13.21.10", {"start": v(35.3, -11.48) * mm, "mid": v(34.11, -11.56) * mm, "end": v(33.32, -12.43) * mm});
            skArc(sketch, "E13.21.11", {"start": v(36.57, -11.76) * mm, "mid": v(37.71, -11.59) * mm, "end": v(38.83, -11.28) * mm});
            skArc(sketch, "E13.22.0", {"start": v(35.53, 1.53) * mm, "mid": v(36.02, 0.45) * mm, "end": v(37.11, 0) * mm});
            skLineSegment(sketch, "E13.22.1", {"start": v(37.8, 0) * mm, "end": v(37.11, 0) * mm});
            skArc(sketch, "E13.22.2", {"start": v(38.41, -0.12) * mm, "mid": v(38.1, -0.02) * mm, "end": v(37.8, 0) * mm});
            skArc(sketch, "E13.22.3", {"start": v(38.41, -0.12) * mm, "mid": v(39.45, -0.63) * mm, "end": v(40.41, -1.27) * mm});
            skArc(sketch, "E13.22.4", {"start": v(40.61, -1.68) * mm, "mid": v(40.56, -1.45) * mm, "end": v(40.41, -1.27) * mm});
            skLineSegment(sketch, "E13.22.5", {"start": v(40.61, -1.68) * mm, "end": v(40.61, -2.13) * mm});
            skLineSegment(sketch, "E13.22.6", {"start": v(40.57, -2.58) * mm, "end": v(40.61, -2.13) * mm});
            skArc(sketch, "E13.22.7", {"start": v(40.32, -2.96) * mm, "mid": v(40.5, -2.8) * mm, "end": v(40.57, -2.58) * mm});
            skArc(sketch, "E13.22.8", {"start": v(37.58, -3.96) * mm, "mid": v(37.9, -3.96) * mm, "end": v(38.22, -3.9) * mm});
            skLineSegment(sketch, "E13.22.9", {"start": v(37.58, -3.96) * mm, "end": v(36.9, -3.89) * mm});
            skArc(sketch, "E13.22.10", {"start": v(36.9, -3.89) * mm, "mid": v(35.77, -4.21) * mm, "end": v(35.17, -5.23) * mm});
            skArc(sketch, "E13.22.11", {"start": v(38.22, -3.9) * mm, "mid": v(39.3, -3.5) * mm, "end": v(40.32, -2.96) * mm});
            skArc(sketch, "E13.23.0", {"start": v(34.43, 8.88) * mm, "mid": v(35.13, 7.93) * mm, "end": v(36.3, 7.72) * mm});
            skLineSegment(sketch, "E13.23.1", {"start": v(36.96, 7.87) * mm, "end": v(36.3, 7.72) * mm});
            skArc(sketch, "E13.23.2", {"start": v(37.6, 7.87) * mm, "mid": v(37.28, 7.9) * mm, "end": v(36.96, 7.87) * mm});
            skArc(sketch, "E13.23.3", {"start": v(37.6, 7.87) * mm, "mid": v(38.72, 7.58) * mm, "end": v(39.8, 7.16) * mm});
            skArc(sketch, "E13.23.4", {"start": v(40.08, 6.8) * mm, "mid": v(39.98, 7.01) * mm, "end": v(39.8, 7.16) * mm});
            skLineSegment(sketch, "E13.23.5", {"start": v(40.08, 6.8) * mm, "end": v(40.17, 6.36) * mm});
            skLineSegment(sketch, "E13.23.6", {"start": v(40.22, 5.92) * mm, "end": v(40.17, 6.36) * mm});
            skArc(sketch, "E13.23.7", {"start": v(40.06, 5.5) * mm, "mid": v(40.19, 5.68) * mm, "end": v(40.22, 5.92) * mm});
            skArc(sketch, "E13.23.8", {"start": v(37.59, 3.94) * mm, "mid": v(37.9, 4) * mm, "end": v(38.2, 4.13) * mm});
            skLineSegment(sketch, "E13.23.9", {"start": v(37.59, 3.94) * mm, "end": v(36.91, 3.87) * mm});
            skArc(sketch, "E13.23.10", {"start": v(36.91, 3.87) * mm, "mid": v(35.86, 3.32) * mm, "end": v(35.5, 2.2) * mm});
            skArc(sketch, "E13.23.11", {"start": v(38.2, 4.13) * mm, "mid": v(39.17, 4.75) * mm, "end": v(40.06, 5.5) * mm});
            skArc(sketch, "E13.24.0", {"start": v(31.83, 15.85) * mm, "mid": v(32.72, 15.06) * mm, "end": v(33.9, 15.1) * mm});
            skLineSegment(sketch, "E13.24.1", {"start": v(34.52, 15.38) * mm, "end": v(33.9, 15.1) * mm});
            skArc(sketch, "E13.24.2", {"start": v(35.14, 15.52) * mm, "mid": v(34.82, 15.48) * mm, "end": v(34.52, 15.38) * mm});
            skArc(sketch, "E13.24.3", {"start": v(35.14, 15.52) * mm, "mid": v(36.3, 15.46) * mm, "end": v(37.44, 15.27) * mm});
            skArc(sketch, "E13.24.4", {"start": v(37.79, 14.99) * mm, "mid": v(37.65, 15.17) * mm, "end": v(37.44, 15.27) * mm});
            skLineSegment(sketch, "E13.24.5", {"start": v(37.79, 14.99) * mm, "end": v(37.97, 14.58) * mm});
            skLineSegment(sketch, "E13.24.6", {"start": v(38.1, 14.15) * mm, "end": v(37.97, 14.58) * mm});
            skArc(sketch, "E13.24.7", {"start": v(38.04, 13.7) * mm, "mid": v(38.13, 13.92) * mm, "end": v(38.1, 14.15) * mm});
            skArc(sketch, "E13.24.8", {"start": v(35.94, 11.67) * mm, "mid": v(36.24, 11.8) * mm, "end": v(36.5, 11.98) * mm});
            skLineSegment(sketch, "E13.24.9", {"start": v(35.94, 11.67) * mm, "end": v(35.3, 11.46) * mm});
            skArc(sketch, "E13.24.10", {"start": v(35.3, 11.46) * mm, "mid": v(34.4, 10.7) * mm, "end": v(34.26, 9.53) * mm});
            skArc(sketch, "E13.24.11", {"start": v(36.5, 11.98) * mm, "mid": v(37.32, 12.8) * mm, "end": v(38.04, 13.7) * mm});
            skArc(sketch, "E13.25.0", {"start": v(27.84, 22.12) * mm, "mid": v(28.87, 21.53) * mm, "end": v(30.02, 21.82) * mm});
            skLineSegment(sketch, "E13.25.1", {"start": v(30.57, 22.22) * mm, "end": v(30.02, 21.82) * mm});
            skArc(sketch, "E13.25.2", {"start": v(31.15, 22.48) * mm, "mid": v(30.84, 22.38) * mm, "end": v(30.57, 22.22) * mm});
            skArc(sketch, "E13.25.3", {"start": v(31.15, 22.48) * mm, "mid": v(32.29, 22.67) * mm, "end": v(33.44, 22.72) * mm});
            skArc(sketch, "E13.25.4", {"start": v(33.85, 22.51) * mm, "mid": v(33.67, 22.67) * mm, "end": v(33.44, 22.72) * mm});
            skLineSegment(sketch, "E13.25.5", {"start": v(33.85, 22.51) * mm, "end": v(34.1, 22.15) * mm});
            skLineSegment(sketch, "E13.25.6", {"start": v(34.33, 21.76) * mm, "end": v(34.1, 22.15) * mm});
            skArc(sketch, "E13.25.7", {"start": v(34.36, 21.3) * mm, "mid": v(34.4, 21.54) * mm, "end": v(34.33, 21.76) * mm});
            skArc(sketch, "E13.25.8", {"start": v(32.73, 18.89) * mm, "mid": v(33, 19.07) * mm, "end": v(33.2, 19.3) * mm});
            skLineSegment(sketch, "E13.25.9", {"start": v(32.73, 18.89) * mm, "end": v(32.15, 18.55) * mm});
            skArc(sketch, "E13.25.10", {"start": v(32.15, 18.55) * mm, "mid": v(31.41, 17.62) * mm, "end": v(31.53, 16.44) * mm});
            skArc(sketch, "E13.25.11", {"start": v(33.2, 19.3) * mm, "mid": v(33.85, 20.27) * mm, "end": v(34.36, 21.3) * mm});
            skArc(sketch, "E13.26.0", {"start": v(22.64, 27.42) * mm, "mid": v(23.76, 27.07) * mm, "end": v(24.83, 27.59) * mm});
            skLineSegment(sketch, "E13.26.1", {"start": v(25.28, 28.1) * mm, "end": v(24.83, 27.59) * mm});
            skArc(sketch, "E13.26.2", {"start": v(25.8, 28.47) * mm, "mid": v(25.52, 28.3) * mm, "end": v(25.28, 28.1) * mm});
            skArc(sketch, "E13.26.3", {"start": v(25.8, 28.47) * mm, "mid": v(26.87, 28.9) * mm, "end": v(27.99, 29.18) * mm});
            skArc(sketch, "E13.26.4", {"start": v(28.42, 29.06) * mm, "mid": v(28.22, 29.17) * mm, "end": v(27.99, 29.18) * mm});
            skLineSegment(sketch, "E13.26.5", {"start": v(28.42, 29.06) * mm, "end": v(28.76, 28.76) * mm});
            skLineSegment(sketch, "E13.26.6", {"start": v(29.06, 28.42) * mm, "end": v(28.76, 28.76) * mm});
            skArc(sketch, "E13.26.7", {"start": v(29.18, 27.99) * mm, "mid": v(29.17, 28.22) * mm, "end": v(29.06, 28.42) * mm});
            skArc(sketch, "E13.26.8", {"start": v(28.1, 25.28) * mm, "mid": v(28.3, 25.52) * mm, "end": v(28.47, 25.8) * mm});
            skLineSegment(sketch, "E13.26.9", {"start": v(28.1, 25.28) * mm, "end": v(27.59, 24.83) * mm});
            skArc(sketch, "E13.26.10", {"start": v(27.59, 24.83) * mm, "mid": v(27.07, 23.76) * mm, "end": v(27.42, 22.64) * mm});
            skArc(sketch, "E13.26.11", {"start": v(28.47, 25.8) * mm, "mid": v(28.9, 26.87) * mm, "end": v(29.18, 27.99) * mm});
            skArc(sketch, "E13.27.0", {"start": v(16.44, 31.53) * mm, "mid": v(17.62, 31.41) * mm, "end": v(18.55, 32.15) * mm});
            skLineSegment(sketch, "E13.27.1", {"start": v(18.89, 32.73) * mm, "end": v(18.55, 32.15) * mm});
            skArc(sketch, "E13.27.2", {"start": v(19.3, 33.2) * mm, "mid": v(19.07, 33) * mm, "end": v(18.89, 32.73) * mm});
            skArc(sketch, "E13.27.3", {"start": v(19.3, 33.2) * mm, "mid": v(20.27, 33.85) * mm, "end": v(21.3, 34.36) * mm});
            skArc(sketch, "E13.27.4", {"start": v(21.76, 34.33) * mm, "mid": v(21.54, 34.4) * mm, "end": v(21.3, 34.36) * mm});
            skLineSegment(sketch, "E13.27.5", {"start": v(21.76, 34.33) * mm, "end": v(22.15, 34.1) * mm});
            skLineSegment(sketch, "E13.27.6", {"start": v(22.51, 33.85) * mm, "end": v(22.15, 34.1) * mm});
            skArc(sketch, "E13.27.7", {"start": v(22.72, 33.44) * mm, "mid": v(22.67, 33.67) * mm, "end": v(22.51, 33.85) * mm});
            skArc(sketch, "E13.27.8", {"start": v(22.22, 30.57) * mm, "mid": v(22.38, 30.84) * mm, "end": v(22.48, 31.15) * mm});
            skLineSegment(sketch, "E13.27.9", {"start": v(22.22, 30.57) * mm, "end": v(21.82, 30.02) * mm});
            skArc(sketch, "E13.27.10", {"start": v(21.82, 30.02) * mm, "mid": v(21.53, 28.87) * mm, "end": v(22.12, 27.84) * mm});
            skArc(sketch, "E13.27.11", {"start": v(22.48, 31.15) * mm, "mid": v(22.67, 32.29) * mm, "end": v(22.72, 33.44) * mm});
            skArc(sketch, "E13.28.0", {"start": v(9.53, 34.26) * mm, "mid": v(10.7, 34.4) * mm, "end": v(11.46, 35.3) * mm});
            skLineSegment(sketch, "E13.28.1", {"start": v(11.67, 35.94) * mm, "end": v(11.46, 35.3) * mm});
            skArc(sketch, "E13.28.2", {"start": v(11.98, 36.5) * mm, "mid": v(11.8, 36.24) * mm, "end": v(11.67, 35.94) * mm});
            skArc(sketch, "E13.28.3", {"start": v(11.98, 36.5) * mm, "mid": v(12.8, 37.32) * mm, "end": v(13.7, 38.04) * mm});
            skArc(sketch, "E13.28.4", {"start": v(14.15, 38.1) * mm, "mid": v(13.92, 38.13) * mm, "end": v(13.7, 38.04) * mm});
            skLineSegment(sketch, "E13.28.5", {"start": v(14.15, 38.1) * mm, "end": v(14.58, 37.97) * mm});
            skLineSegment(sketch, "E13.28.6", {"start": v(14.99, 37.79) * mm, "end": v(14.58, 37.97) * mm});
            skArc(sketch, "E13.28.7", {"start": v(15.27, 37.44) * mm, "mid": v(15.17, 37.65) * mm, "end": v(14.99, 37.79) * mm});
            skArc(sketch, "E13.28.8", {"start": v(15.38, 34.52) * mm, "mid": v(15.48, 34.82) * mm, "end": v(15.52, 35.14) * mm});
            skLineSegment(sketch, "E13.28.9", {"start": v(15.38, 34.52) * mm, "end": v(15.1, 33.9) * mm});
            skArc(sketch, "E13.28.10", {"start": v(15.1, 33.9) * mm, "mid": v(15.06, 32.72) * mm, "end": v(15.85, 31.83) * mm});
            skArc(sketch, "E13.28.11", {"start": v(15.52, 35.14) * mm, "mid": v(15.46, 36.3) * mm, "end": v(15.27, 37.44) * mm});
            skArc(sketch, "E13.29.0", {"start": v(2.2, 35.5) * mm, "mid": v(3.32, 35.86) * mm, "end": v(3.87, 36.91) * mm});
            skLineSegment(sketch, "E13.29.1", {"start": v(3.94, 37.59) * mm, "end": v(3.87, 36.91) * mm});
            skArc(sketch, "E13.29.2", {"start": v(4.13, 38.2) * mm, "mid": v(4, 37.9) * mm, "end": v(3.94, 37.59) * mm});
            skArc(sketch, "E13.29.3", {"start": v(4.13, 38.2) * mm, "mid": v(4.75, 39.17) * mm, "end": v(5.5, 40.06) * mm});
            skArc(sketch, "E13.29.4", {"start": v(5.92, 40.22) * mm, "mid": v(5.68, 40.19) * mm, "end": v(5.5, 40.06) * mm});
            skLineSegment(sketch, "E13.29.5", {"start": v(5.92, 40.22) * mm, "end": v(6.36, 40.17) * mm});
            skLineSegment(sketch, "E13.29.6", {"start": v(6.8, 40.08) * mm, "end": v(6.36, 40.17) * mm});
            skArc(sketch, "E13.29.7", {"start": v(7.16, 39.8) * mm, "mid": v(7.01, 39.98) * mm, "end": v(6.8, 40.08) * mm});
            skArc(sketch, "E13.29.8", {"start": v(7.87, 36.96) * mm, "mid": v(7.9, 37.28) * mm, "end": v(7.87, 37.6) * mm});
            skLineSegment(sketch, "E13.29.9", {"start": v(7.87, 36.96) * mm, "end": v(7.72, 36.3) * mm});
            skArc(sketch, "E13.29.10", {"start": v(7.72, 36.3) * mm, "mid": v(7.93, 35.13) * mm, "end": v(8.88, 34.43) * mm});
            skArc(sketch, "E13.29.11", {"start": v(7.87, 37.6) * mm, "mid": v(7.58, 38.72) * mm, "end": v(7.16, 39.8) * mm});
            skArc(sketch, "E14.trimOffspring", {"start": v(2.2, 35.5) * mm, "mid": v(1.86, 35.51) * mm, "end": v(1.53, 35.53) * mm});
            skArc(sketch, "E15.trimOffspring", {"start": v(9.53, 34.26) * mm, "mid": v(9.2, 34.35) * mm, "end": v(8.88, 34.43) * mm});
            skArc(sketch, "E16.trimOffspring", {"start": v(16.44, 31.53) * mm, "mid": v(16.14, 31.68) * mm, "end": v(15.85, 31.83) * mm});
            skArc(sketch, "E17.trimOffspring", {"start": v(22.64, 27.42) * mm, "mid": v(22.38, 27.64) * mm, "end": v(22.12, 27.84) * mm});
            skArc(sketch, "E18.trimOffspring", {"start": v(27.84, 22.12) * mm, "mid": v(27.64, 22.38) * mm, "end": v(27.42, 22.64) * mm});
            skArc(sketch, "E19.trimOffspring", {"start": v(31.83, 15.85) * mm, "mid": v(31.68, 16.14) * mm, "end": v(31.53, 16.44) * mm});
            skArc(sketch, "E20.trimOffspring", {"start": v(34.43, 8.88) * mm, "mid": v(34.35, 9.2) * mm, "end": v(34.26, 9.53) * mm});
            skArc(sketch, "E21.trimOffspring", {"start": v(35.53, 1.53) * mm, "mid": v(35.51, 1.86) * mm, "end": v(35.5, 2.2) * mm});
            skArc(sketch, "E22.trimOffspring", {"start": v(35.07, -5.9) * mm, "mid": v(35.12, -5.56) * mm, "end": v(35.17, -5.23) * mm});
            skArc(sketch, "E23.trimOffspring", {"start": v(33.08, -13.05) * mm, "mid": v(33.2, -12.74) * mm, "end": v(33.32, -12.43) * mm});
            skArc(sketch, "E24.trimOffspring", {"start": v(29.64, -19.65) * mm, "mid": v(29.82, -19.37) * mm, "end": v(30, -19.09) * mm});
            skArc(sketch, "E25.trimOffspring", {"start": v(24.9, -25.38) * mm, "mid": v(25.14, -25.14) * mm, "end": v(25.38, -24.9) * mm});
            skArc(sketch, "E26.trimOffspring", {"start": v(-33.08, 13.05) * mm, "mid": v(-33.2, 12.74) * mm, "end": v(-33.32, 12.43) * mm});
            skArc(sketch, "E27.trimOffspring", {"start": v(-29.64, 19.65) * mm, "mid": v(-29.82, 19.37) * mm, "end": v(-30, 19.09) * mm});
            skArc(sketch, "E28.trimOffspring", {"start": v(-24.9, 25.38) * mm, "mid": v(-25.14, 25.14) * mm, "end": v(-25.38, 24.9) * mm});
            skArc(sketch, "E29.trimOffspring", {"start": v(-19.09, 30) * mm, "mid": v(-19.37, 29.82) * mm, "end": v(-19.65, 29.64) * mm});
            skArc(sketch, "E30.trimOffspring", {"start": v(-12.43, 33.32) * mm, "mid": v(-12.74, 33.2) * mm, "end": v(-13.05, 33.08) * mm});
            skArc(sketch, "E31.trimOffspring", {"start": v(-34.43, -8.88) * mm, "mid": v(-34.35, -9.2) * mm, "end": v(-34.26, -9.53) * mm});
            skArc(sketch, "E32.trimOffspring", {"start": v(-35.53, -1.53) * mm, "mid": v(-35.51, -1.86) * mm, "end": v(-35.5, -2.2) * mm});
            skArc(sketch, "E33.trimOffspring", {"start": v(-35.07, 5.9) * mm, "mid": v(-35.12, 5.56) * mm, "end": v(-35.17, 5.23) * mm});
            skArc(sketch, "E34.trimOffspring", {"start": v(-31.83, -15.85) * mm, "mid": v(-31.68, -16.14) * mm, "end": v(-31.53, -16.44) * mm});
            skArc(sketch, "E35.trimOffspring", {"start": v(-27.84, -22.12) * mm, "mid": v(-27.64, -22.38) * mm, "end": v(-27.42, -22.64) * mm});
            skArc(sketch, "E36.trimOffspring", {"start": v(-22.64, -27.42) * mm, "mid": v(-22.38, -27.64) * mm, "end": v(-22.12, -27.84) * mm});
            skArc(sketch, "E37.trimOffspring", {"start": v(-16.44, -31.53) * mm, "mid": v(-16.14, -31.68) * mm, "end": v(-15.85, -31.83) * mm});
            skArc(sketch, "E38.trimOffspring", {"start": v(-9.53, -34.26) * mm, "mid": v(-9.2, -34.35) * mm, "end": v(-8.88, -34.43) * mm});
            skArc(sketch, "E39.trimOffspring", {"start": v(-2.2, -35.5) * mm, "mid": v(-1.86, -35.51) * mm, "end": v(-1.53, -35.53) * mm});
            skArc(sketch, "E40.trimOffspring", {"start": v(5.23, -35.17) * mm, "mid": v(5.56, -35.12) * mm, "end": v(5.9, -35.07) * mm});
            skArc(sketch, "E41.trimOffspring", {"start": v(12.43, -33.32) * mm, "mid": v(12.74, -33.2) * mm, "end": v(13.05, -33.08) * mm});
            skArc(sketch, "E42.trimOffspring", {"start": v(19.09, -30) * mm, "mid": v(19.37, -29.82) * mm, "end": v(19.65, -29.64) * mm});
            skSolve(sketch);
        }
        {
            var Q0;
            Q0=makeQuery(id+"F0.imprint","IMPRINT",FACE,{"disambiguationData":[TD([[makeQuery(id+"F0.imprint","IMPRINT",EDGE,{"derivedFrom":sQuery(id+"F0.wireOp",EDGE,"E0")}),1.0]])]});
            cPlane(context, id + "F1", {"entities" : qUnion([Q0]), "cplaneType" : CPlaneType.OFFSET, "offset" : 22 * mm, "width" : 152.4 * mm, "height" : 152.4 * mm});
        }
        {
            var Q0;
            Q0=qCreatedBy(id+"F1.planeOp",FACE);
            var sketch = newSketch(context, id + "F2", { "sketchPlane" : qUnion([Q0])});
            skArc(sketch, "E43", {"start": v(-3.25, 23.48) * mm, "mid": v(-3.7, 23.41) * mm, "end": v(-4.17, 23.34) * mm});
            skArc(sketch, "E44.trimOffspring", {"start": v(-0.14, 25.74) * mm, "mid": v(-0.44, 26.32) * mm, "end": v(-0.8, 26.87) * mm});
            skLineSegment(sketch, "E45", {"start": v(0, 25.08) * mm, "end": v(0, 24.49) * mm});
            skLineSegment(sketch, "E46", {"start": v(-1.2, 27.08) * mm, "end": v(-1.42, 27.08) * mm});
            skLineSegment(sketch, "E47.MirrorCS", {"start": v(-1.63, 27.05) * mm, "end": v(-1.42, 27.08) * mm});
            skArc(sketch, "E48.MirrorCS", {"start": v(-2.56, 25.61) * mm, "mid": v(-2.32, 26.22) * mm, "end": v(-2.02, 26.8) * mm});
            skLineSegment(sketch, "E49.MirrorCS", {"start": v(-2.63, 24.95) * mm, "end": v(-2.57, 24.35) * mm});
            skPoint(sketch, "E50.visualSharp", {"position": v(-1.88, 27.03) * mm});
            skArc(sketch, "E50.filletArc", {"start": v(-1.63, 27.05) * mm, "mid": v(-1.86, 26.98) * mm, "end": v(-2.02, 26.8) * mm});
            skPoint(sketch, "E51.visualSharp", {"position": v(-0.95, 27.08) * mm});
            skArc(sketch, "E51.filletArc", {"start": v(-0.8, 26.87) * mm, "mid": v(-0.97, 27.02) * mm, "end": v(-1.2, 27.08) * mm});
            skPoint(sketch, "E52.visualSharp", {"position": v(-2.66, 25.26) * mm});
            skArc(sketch, "E52.filletArc", {"start": v(-2.56, 25.61) * mm, "mid": v(-2.63, 25.28) * mm, "end": v(-2.63, 24.95) * mm});
            skPoint(sketch, "E53.visualSharp", {"position": v(0, 25.4) * mm});
            skArc(sketch, "E53.filletArc", {"start": v(0, 25.08) * mm, "mid": v(-0.03, 25.42) * mm, "end": v(-0.14, 25.74) * mm});
            skPoint(sketch, "E54.visualSharp", {"position": v(-2.48, 23.58) * mm});
            skArc(sketch, "E54.filletArc", {"start": v(-3.25, 23.48) * mm, "mid": v(-2.73, 23.78) * mm, "end": v(-2.57, 24.35) * mm});
            skPoint(sketch, "E55.visualSharp", {"position": v(0, 23.7) * mm});
            skArc(sketch, "E55.filletArc", {"start": v(0, 24.49) * mm, "mid": v(0.23, 23.94) * mm, "end": v(0.77, 23.7) * mm});
            skArc(sketch, "E56.1.0", {"start": v(-8.06, 22.3) * mm, "mid": v(-7.61, 22.7) * mm, "end": v(-7.57, 23.29) * mm});
            skLineSegment(sketch, "E56.1.1", {"start": v(-7.76, 23.85) * mm, "end": v(-7.57, 23.29) * mm});
            skArc(sketch, "E56.1.2", {"start": v(-7.82, 24.52) * mm, "mid": v(-7.83, 24.18) * mm, "end": v(-7.76, 23.85) * mm});
            skArc(sketch, "E56.1.3", {"start": v(-7.82, 24.52) * mm, "mid": v(-7.72, 25.17) * mm, "end": v(-7.55, 25.8) * mm});
            skArc(sketch, "E56.1.4", {"start": v(-7.22, 26.12) * mm, "mid": v(-7.42, 26) * mm, "end": v(-7.55, 25.8) * mm});
            skLineSegment(sketch, "E56.1.5", {"start": v(-7.22, 26.12) * mm, "end": v(-7.02, 26.19) * mm});
            skLineSegment(sketch, "E56.1.6", {"start": v(-6.8, 26.23) * mm, "end": v(-7.02, 26.19) * mm});
            skArc(sketch, "E56.1.7", {"start": v(-6.36, 26.12) * mm, "mid": v(-6.57, 26.23) * mm, "end": v(-6.8, 26.23) * mm});
            skArc(sketch, "E56.1.8", {"start": v(-5.48, 25.15) * mm, "mid": v(-5.9, 25.65) * mm, "end": v(-6.36, 26.12) * mm});
            skArc(sketch, "E56.1.9", {"start": v(-5.2, 24.54) * mm, "mid": v(-5.31, 24.86) * mm, "end": v(-5.48, 25.15) * mm});
            skLineSegment(sketch, "E56.1.10", {"start": v(-5.2, 24.54) * mm, "end": v(-5.09, 23.95) * mm});
            skArc(sketch, "E56.1.11", {"start": v(-5.09, 23.95) * mm, "mid": v(-4.75, 23.46) * mm, "end": v(-4.17, 23.34) * mm});
            skArc(sketch, "E56.2.0", {"start": v(-12.52, 20.13) * mm, "mid": v(-12.17, 20.61) * mm, "end": v(-12.25, 21.2) * mm});
            skLineSegment(sketch, "E56.2.1", {"start": v(-12.55, 21.72) * mm, "end": v(-12.25, 21.2) * mm});
            skArc(sketch, "E56.2.2", {"start": v(-12.75, 22.36) * mm, "mid": v(-12.68, 22.03) * mm, "end": v(-12.55, 21.72) * mm});
            skArc(sketch, "E56.2.3", {"start": v(-12.75, 22.36) * mm, "mid": v(-12.78, 23.01) * mm, "end": v(-12.75, 23.67) * mm});
            skArc(sketch, "E56.2.4", {"start": v(-12.5, 24.05) * mm, "mid": v(-12.67, 23.89) * mm, "end": v(-12.75, 23.67) * mm});
            skLineSegment(sketch, "E56.2.5", {"start": v(-12.5, 24.05) * mm, "end": v(-12.3, 24.16) * mm});
            skLineSegment(sketch, "E56.2.6", {"start": v(-12.11, 24.25) * mm, "end": v(-12.3, 24.16) * mm});
            skArc(sketch, "E56.2.7", {"start": v(-11.65, 24.22) * mm, "mid": v(-11.88, 24.29) * mm, "end": v(-12.11, 24.25) * mm});
            skArc(sketch, "E56.2.8", {"start": v(-10.6, 23.46) * mm, "mid": v(-11.1, 23.87) * mm, "end": v(-11.65, 24.22) * mm});
            skArc(sketch, "E56.2.9", {"start": v(-10.2, 22.92) * mm, "mid": v(-10.37, 23.2) * mm, "end": v(-10.6, 23.46) * mm});
            skLineSegment(sketch, "E56.2.10", {"start": v(-10.2, 22.92) * mm, "end": v(-9.95, 22.37) * mm});
            skArc(sketch, "E56.2.11", {"start": v(-9.95, 22.37) * mm, "mid": v(-9.53, 21.96) * mm, "end": v(-8.93, 21.96) * mm});
            skArc(sketch, "E56.3.0", {"start": v(-16.43, 17.1) * mm, "mid": v(-16.19, 17.63) * mm, "end": v(-16.39, 18.2) * mm});
            skLineSegment(sketch, "E56.3.1", {"start": v(-16.79, 18.64) * mm, "end": v(-16.39, 18.2) * mm});
            skArc(sketch, "E56.3.2", {"start": v(-17.12, 19.22) * mm, "mid": v(-16.99, 18.9) * mm, "end": v(-16.79, 18.64) * mm});
            skArc(sketch, "E56.3.3", {"start": v(-17.12, 19.22) * mm, "mid": v(-17.29, 19.85) * mm, "end": v(-17.39, 20.5) * mm});
            skArc(sketch, "E56.3.4", {"start": v(-17.22, 20.93) * mm, "mid": v(-17.36, 20.73) * mm, "end": v(-17.39, 20.5) * mm});
            skLineSegment(sketch, "E56.3.5", {"start": v(-17.22, 20.93) * mm, "end": v(-17.06, 21.07) * mm});
            skLineSegment(sketch, "E56.3.6", {"start": v(-16.89, 21.2) * mm, "end": v(-17.06, 21.07) * mm});
            skArc(sketch, "E56.3.7", {"start": v(-16.44, 21.27) * mm, "mid": v(-16.67, 21.29) * mm, "end": v(-16.89, 21.2) * mm});
            skArc(sketch, "E56.3.8", {"start": v(-15.24, 20.74) * mm, "mid": v(-15.82, 21.04) * mm, "end": v(-16.44, 21.27) * mm});
            skArc(sketch, "E56.3.9", {"start": v(-14.74, 20.3) * mm, "mid": v(-14.96, 20.55) * mm, "end": v(-15.24, 20.74) * mm});
            skLineSegment(sketch, "E56.3.10", {"start": v(-14.74, 20.3) * mm, "end": v(-14.39, 19.81) * mm});
            skArc(sketch, "E56.3.11", {"start": v(-14.39, 19.81) * mm, "mid": v(-13.88, 19.5) * mm, "end": v(-13.3, 19.62) * mm});
            skArc(sketch, "E56.4.0", {"start": v(-19.62, 13.3) * mm, "mid": v(-19.5, 13.88) * mm, "end": v(-19.81, 14.39) * mm});
            skLineSegment(sketch, "E56.4.1", {"start": v(-20.3, 14.74) * mm, "end": v(-19.81, 14.39) * mm});
            skArc(sketch, "E56.4.2", {"start": v(-20.74, 15.24) * mm, "mid": v(-20.55, 14.96) * mm, "end": v(-20.3, 14.74) * mm});
            skArc(sketch, "E56.4.3", {"start": v(-20.74, 15.24) * mm, "mid": v(-21.04, 15.82) * mm, "end": v(-21.27, 16.44) * mm});
            skArc(sketch, "E56.4.4", {"start": v(-21.2, 16.89) * mm, "mid": v(-21.29, 16.67) * mm, "end": v(-21.27, 16.44) * mm});
            skLineSegment(sketch, "E56.4.5", {"start": v(-21.2, 16.89) * mm, "end": v(-21.07, 17.06) * mm});
            skLineSegment(sketch, "E56.4.6", {"start": v(-20.93, 17.22) * mm, "end": v(-21.07, 17.06) * mm});
            skArc(sketch, "E56.4.7", {"start": v(-20.5, 17.39) * mm, "mid": v(-20.73, 17.36) * mm, "end": v(-20.93, 17.22) * mm});
            skArc(sketch, "E56.4.8", {"start": v(-19.22, 17.12) * mm, "mid": v(-19.85, 17.29) * mm, "end": v(-20.5, 17.39) * mm});
            skArc(sketch, "E56.4.9", {"start": v(-18.64, 16.79) * mm, "mid": v(-18.9, 16.99) * mm, "end": v(-19.22, 17.12) * mm});
            skLineSegment(sketch, "E56.4.10", {"start": v(-18.64, 16.79) * mm, "end": v(-18.2, 16.39) * mm});
            skArc(sketch, "E56.4.11", {"start": v(-18.2, 16.39) * mm, "mid": v(-17.63, 16.19) * mm, "end": v(-17.1, 16.43) * mm});
            skArc(sketch, "E56.5.0", {"start": v(-21.96, 8.93) * mm, "mid": v(-21.96, 9.53) * mm, "end": v(-22.37, 9.95) * mm});
            skLineSegment(sketch, "E56.5.1", {"start": v(-22.92, 10.2) * mm, "end": v(-22.37, 9.95) * mm});
            skArc(sketch, "E56.5.2", {"start": v(-23.46, 10.6) * mm, "mid": v(-23.2, 10.37) * mm, "end": v(-22.92, 10.2) * mm});
            skArc(sketch, "E56.5.3", {"start": v(-23.46, 10.6) * mm, "mid": v(-23.87, 11.1) * mm, "end": v(-24.22, 11.65) * mm});
            skArc(sketch, "E56.5.4", {"start": v(-24.25, 12.11) * mm, "mid": v(-24.29, 11.88) * mm, "end": v(-24.22, 11.65) * mm});
            skLineSegment(sketch, "E56.5.5", {"start": v(-24.25, 12.11) * mm, "end": v(-24.16, 12.3) * mm});
            skLineSegment(sketch, "E56.5.6", {"start": v(-24.05, 12.5) * mm, "end": v(-24.16, 12.3) * mm});
            skArc(sketch, "E56.5.7", {"start": v(-23.67, 12.75) * mm, "mid": v(-23.89, 12.67) * mm, "end": v(-24.05, 12.5) * mm});
            skArc(sketch, "E56.5.8", {"start": v(-22.36, 12.75) * mm, "mid": v(-23.01, 12.78) * mm, "end": v(-23.67, 12.75) * mm});
            skArc(sketch, "E56.5.9", {"start": v(-21.72, 12.55) * mm, "mid": v(-22.03, 12.68) * mm, "end": v(-22.36, 12.75) * mm});
            skLineSegment(sketch, "E56.5.10", {"start": v(-21.72, 12.55) * mm, "end": v(-21.2, 12.25) * mm});
            skArc(sketch, "E56.5.11", {"start": v(-21.2, 12.25) * mm, "mid": v(-20.61, 12.17) * mm, "end": v(-20.13, 12.52) * mm});
            skArc(sketch, "E56.6.0", {"start": v(-23.34, 4.17) * mm, "mid": v(-23.46, 4.75) * mm, "end": v(-23.95, 5.09) * mm});
            skLineSegment(sketch, "E56.6.1", {"start": v(-24.54, 5.2) * mm, "end": v(-23.95, 5.09) * mm});
            skArc(sketch, "E56.6.2", {"start": v(-25.15, 5.48) * mm, "mid": v(-24.86, 5.31) * mm, "end": v(-24.54, 5.2) * mm});
            skArc(sketch, "E56.6.3", {"start": v(-25.15, 5.48) * mm, "mid": v(-25.65, 5.9) * mm, "end": v(-26.12, 6.36) * mm});
            skArc(sketch, "E56.6.4", {"start": v(-26.23, 6.8) * mm, "mid": v(-26.23, 6.57) * mm, "end": v(-26.12, 6.36) * mm});
            skLineSegment(sketch, "E56.6.5", {"start": v(-26.23, 6.8) * mm, "end": v(-26.19, 7.02) * mm});
            skLineSegment(sketch, "E56.6.6", {"start": v(-26.12, 7.22) * mm, "end": v(-26.19, 7.02) * mm});
            skArc(sketch, "E56.6.7", {"start": v(-25.8, 7.55) * mm, "mid": v(-26, 7.42) * mm, "end": v(-26.12, 7.22) * mm});
            skArc(sketch, "E56.6.8", {"start": v(-24.52, 7.82) * mm, "mid": v(-25.17, 7.72) * mm, "end": v(-25.8, 7.55) * mm});
            skArc(sketch, "E56.6.9", {"start": v(-23.85, 7.76) * mm, "mid": v(-24.18, 7.83) * mm, "end": v(-24.52, 7.82) * mm});
            skLineSegment(sketch, "E56.6.10", {"start": v(-23.85, 7.76) * mm, "end": v(-23.29, 7.57) * mm});
            skArc(sketch, "E56.6.11", {"start": v(-23.29, 7.57) * mm, "mid": v(-22.7, 7.61) * mm, "end": v(-22.3, 8.06) * mm});
            skArc(sketch, "E56.7.0", {"start": v(-23.7, -0.77) * mm, "mid": v(-23.94, -0.23) * mm, "end": v(-24.49, 0) * mm});
            skLineSegment(sketch, "E56.7.1", {"start": v(-25.08, 0) * mm, "end": v(-24.49, 0) * mm});
            skArc(sketch, "E56.7.2", {"start": v(-25.74, 0.14) * mm, "mid": v(-25.42, 0.03) * mm, "end": v(-25.08, 0) * mm});
            skArc(sketch, "E56.7.3", {"start": v(-25.74, 0.14) * mm, "mid": v(-26.32, 0.44) * mm, "end": v(-26.87, 0.8) * mm});
            skArc(sketch, "E56.7.4", {"start": v(-27.08, 1.2) * mm, "mid": v(-27.02, 0.97) * mm, "end": v(-26.87, 0.8) * mm});
            skLineSegment(sketch, "E56.7.5", {"start": v(-27.08, 1.2) * mm, "end": v(-27.08, 1.42) * mm});
            skLineSegment(sketch, "E56.7.6", {"start": v(-27.05, 1.63) * mm, "end": v(-27.08, 1.42) * mm});
            skArc(sketch, "E56.7.7", {"start": v(-26.8, 2.02) * mm, "mid": v(-26.98, 1.86) * mm, "end": v(-27.05, 1.63) * mm});
            skArc(sketch, "E56.7.8", {"start": v(-25.61, 2.56) * mm, "mid": v(-26.22, 2.32) * mm, "end": v(-26.8, 2.02) * mm});
            skArc(sketch, "E56.7.9", {"start": v(-24.95, 2.63) * mm, "mid": v(-25.28, 2.63) * mm, "end": v(-25.61, 2.56) * mm});
            skLineSegment(sketch, "E56.7.10", {"start": v(-24.95, 2.63) * mm, "end": v(-24.35, 2.57) * mm});
            skArc(sketch, "E56.7.11", {"start": v(-24.35, 2.57) * mm, "mid": v(-23.78, 2.73) * mm, "end": v(-23.48, 3.25) * mm});
            skArc(sketch, "E56.8.0", {"start": v(-23.02, -5.68) * mm, "mid": v(-23.36, -5.2) * mm, "end": v(-23.95, -5.1) * mm});
            skLineSegment(sketch, "E56.8.1", {"start": v(-24.53, -5.22) * mm, "end": v(-23.95, -5.1) * mm});
            skArc(sketch, "E56.8.2", {"start": v(-25.2, -5.22) * mm, "mid": v(-24.87, -5.26) * mm, "end": v(-24.53, -5.22) * mm});
            skArc(sketch, "E56.8.3", {"start": v(-25.2, -5.22) * mm, "mid": v(-25.84, -5.05) * mm, "end": v(-26.45, -4.8) * mm});
            skArc(sketch, "E56.8.4", {"start": v(-26.74, -4.45) * mm, "mid": v(-26.63, -4.66) * mm, "end": v(-26.45, -4.8) * mm});
            skLineSegment(sketch, "E56.8.5", {"start": v(-26.74, -4.45) * mm, "end": v(-26.78, -4.24) * mm});
            skLineSegment(sketch, "E56.8.6", {"start": v(-26.8, -4.03) * mm, "end": v(-26.78, -4.24) * mm});
            skArc(sketch, "E56.8.7", {"start": v(-26.64, -3.6) * mm, "mid": v(-26.77, -3.8) * mm, "end": v(-26.8, -4.03) * mm});
            skArc(sketch, "E56.8.8", {"start": v(-25.58, -2.82) * mm, "mid": v(-26.13, -3.18) * mm, "end": v(-26.64, -3.6) * mm});
            skArc(sketch, "E56.8.9", {"start": v(-24.95, -2.62) * mm, "mid": v(-25.28, -2.69) * mm, "end": v(-25.58, -2.82) * mm});
            skLineSegment(sketch, "E56.8.10", {"start": v(-24.95, -2.62) * mm, "end": v(-24.35, -2.55) * mm});
            skArc(sketch, "E56.8.11", {"start": v(-24.35, -2.55) * mm, "mid": v(-23.83, -2.27) * mm, "end": v(-23.65, -1.7) * mm});
            skArc(sketch, "E56.9.0", {"start": v(-21.33, -10.34) * mm, "mid": v(-21.77, -9.94) * mm, "end": v(-22.37, -9.97) * mm});
            skLineSegment(sketch, "E56.9.1", {"start": v(-22.91, -10.2) * mm, "end": v(-22.37, -9.97) * mm});
            skArc(sketch, "E56.9.2", {"start": v(-23.57, -10.34) * mm, "mid": v(-23.23, -10.31) * mm, "end": v(-22.91, -10.2) * mm});
            skArc(sketch, "E56.9.3", {"start": v(-23.57, -10.34) * mm, "mid": v(-24.22, -10.3) * mm, "end": v(-24.87, -10.2) * mm});
            skArc(sketch, "E56.9.4", {"start": v(-25.23, -9.91) * mm, "mid": v(-25.08, -10.1) * mm, "end": v(-24.87, -10.2) * mm});
            skLineSegment(sketch, "E56.9.5", {"start": v(-25.23, -9.91) * mm, "end": v(-25.31, -9.72) * mm});
            skLineSegment(sketch, "E56.9.6", {"start": v(-25.38, -9.51) * mm, "end": v(-25.31, -9.72) * mm});
            skArc(sketch, "E56.9.7", {"start": v(-25.3, -9.06) * mm, "mid": v(-25.4, -9.28) * mm, "end": v(-25.38, -9.51) * mm});
            skArc(sketch, "E56.9.8", {"start": v(-24.44, -8.08) * mm, "mid": v(-24.9, -8.55) * mm, "end": v(-25.3, -9.06) * mm});
            skArc(sketch, "E56.9.9", {"start": v(-23.86, -7.75) * mm, "mid": v(-24.16, -7.88) * mm, "end": v(-24.44, -8.08) * mm});
            skLineSegment(sketch, "E56.9.10", {"start": v(-23.86, -7.75) * mm, "end": v(-23.3, -7.56) * mm});
            skArc(sketch, "E56.9.11", {"start": v(-23.3, -7.56) * mm, "mid": v(-22.83, -7.18) * mm, "end": v(-22.77, -6.59) * mm});
            skArc(sketch, "E56.10.0", {"start": v(-18.71, -14.55) * mm, "mid": v(-19.23, -14.25) * mm, "end": v(-19.8, -14.4) * mm});
            skLineSegment(sketch, "E56.10.1", {"start": v(-20.29, -14.75) * mm, "end": v(-19.8, -14.4) * mm});
            skArc(sketch, "E56.10.2", {"start": v(-20.9, -15.02) * mm, "mid": v(-20.58, -14.92) * mm, "end": v(-20.29, -14.75) * mm});
            skArc(sketch, "E56.10.3", {"start": v(-20.9, -15.02) * mm, "mid": v(-21.55, -15.12) * mm, "end": v(-22.2, -15.15) * mm});
            skArc(sketch, "E56.10.4", {"start": v(-22.61, -14.94) * mm, "mid": v(-22.43, -15.1) * mm, "end": v(-22.2, -15.15) * mm});
            skLineSegment(sketch, "E56.10.5", {"start": v(-22.61, -14.94) * mm, "end": v(-22.74, -14.77) * mm});
            skLineSegment(sketch, "E56.10.6", {"start": v(-22.85, -14.58) * mm, "end": v(-22.74, -14.77) * mm});
            skArc(sketch, "E56.10.7", {"start": v(-22.87, -14.12) * mm, "mid": v(-22.91, -14.35) * mm, "end": v(-22.85, -14.58) * mm});
            skArc(sketch, "E56.10.8", {"start": v(-22.22, -12.99) * mm, "mid": v(-22.58, -13.54) * mm, "end": v(-22.87, -14.12) * mm});
            skArc(sketch, "E56.10.9", {"start": v(-21.73, -12.54) * mm, "mid": v(-22, -12.73) * mm, "end": v(-22.22, -12.99) * mm});
            skLineSegment(sketch, "E56.10.10", {"start": v(-21.73, -12.54) * mm, "end": v(-21.2, -12.24) * mm});
            skArc(sketch, "E56.10.11", {"start": v(-21.2, -12.24) * mm, "mid": v(-20.84, -11.77) * mm, "end": v(-20.9, -11.18) * mm});
            skArc(sketch, "E56.11.0", {"start": v(-15.28, -18.13) * mm, "mid": v(-15.85, -17.94) * mm, "end": v(-16.38, -18.2) * mm});
            skLineSegment(sketch, "E56.11.1", {"start": v(-16.78, -18.64) * mm, "end": v(-16.38, -18.2) * mm});
            skArc(sketch, "E56.11.2", {"start": v(-17.32, -19.04) * mm, "mid": v(-17.03, -18.87) * mm, "end": v(-16.78, -18.64) * mm});
            skArc(sketch, "E56.11.3", {"start": v(-17.32, -19.04) * mm, "mid": v(-17.94, -19.27) * mm, "end": v(-18.57, -19.44) * mm});
            skArc(sketch, "E56.11.4", {"start": v(-19.01, -19.32) * mm, "mid": v(-18.8, -19.43) * mm, "end": v(-18.57, -19.44) * mm});
            skLineSegment(sketch, "E56.11.5", {"start": v(-19.01, -19.32) * mm, "end": v(-19.17, -19.17) * mm});
            skLineSegment(sketch, "E56.11.6", {"start": v(-19.32, -19.01) * mm, "end": v(-19.17, -19.17) * mm});
            skArc(sketch, "E56.11.7", {"start": v(-19.44, -18.57) * mm, "mid": v(-19.43, -18.8) * mm, "end": v(-19.32, -19.01) * mm});
            skArc(sketch, "E56.11.8", {"start": v(-19.04, -17.32) * mm, "mid": v(-19.27, -17.94) * mm, "end": v(-19.44, -18.57) * mm});
            skArc(sketch, "E56.11.9", {"start": v(-18.64, -16.78) * mm, "mid": v(-18.87, -17.03) * mm, "end": v(-19.04, -17.32) * mm});
            skLineSegment(sketch, "E56.11.10", {"start": v(-18.64, -16.78) * mm, "end": v(-18.2, -16.38) * mm});
            skArc(sketch, "E56.11.11", {"start": v(-18.2, -16.38) * mm, "mid": v(-17.94, -15.85) * mm, "end": v(-18.13, -15.28) * mm});
            skArc(sketch, "E56.12.0", {"start": v(-11.18, -20.9) * mm, "mid": v(-11.77, -20.84) * mm, "end": v(-12.24, -21.2) * mm});
            skLineSegment(sketch, "E56.12.1", {"start": v(-12.54, -21.73) * mm, "end": v(-12.24, -21.2) * mm});
            skArc(sketch, "E56.12.2", {"start": v(-12.99, -22.22) * mm, "mid": v(-12.73, -22) * mm, "end": v(-12.54, -21.73) * mm});
            skArc(sketch, "E56.12.3", {"start": v(-12.99, -22.22) * mm, "mid": v(-13.54, -22.58) * mm, "end": v(-14.12, -22.87) * mm});
            skArc(sketch, "E56.12.4", {"start": v(-14.58, -22.85) * mm, "mid": v(-14.35, -22.91) * mm, "end": v(-14.12, -22.87) * mm});
            skLineSegment(sketch, "E56.12.5", {"start": v(-14.58, -22.85) * mm, "end": v(-14.77, -22.74) * mm});
            skLineSegment(sketch, "E56.12.6", {"start": v(-14.94, -22.61) * mm, "end": v(-14.77, -22.74) * mm});
            skArc(sketch, "E56.12.7", {"start": v(-15.15, -22.2) * mm, "mid": v(-15.1, -22.43) * mm, "end": v(-14.94, -22.61) * mm});
            skArc(sketch, "E56.12.8", {"start": v(-15.02, -20.9) * mm, "mid": v(-15.12, -21.55) * mm, "end": v(-15.15, -22.2) * mm});
            skArc(sketch, "E56.12.9", {"start": v(-14.75, -20.29) * mm, "mid": v(-14.92, -20.58) * mm, "end": v(-15.02, -20.9) * mm});
            skLineSegment(sketch, "E56.12.10", {"start": v(-14.75, -20.29) * mm, "end": v(-14.4, -19.8) * mm});
            skArc(sketch, "E56.12.11", {"start": v(-14.4, -19.8) * mm, "mid": v(-14.25, -19.23) * mm, "end": v(-14.55, -18.71) * mm});
            skArc(sketch, "E56.13.0", {"start": v(-6.59, -22.77) * mm, "mid": v(-7.18, -22.83) * mm, "end": v(-7.56, -23.3) * mm});
            skLineSegment(sketch, "E56.13.1", {"start": v(-7.75, -23.86) * mm, "end": v(-7.56, -23.3) * mm});
            skArc(sketch, "E56.13.2", {"start": v(-8.08, -24.44) * mm, "mid": v(-7.88, -24.16) * mm, "end": v(-7.75, -23.86) * mm});
            skArc(sketch, "E56.13.3", {"start": v(-8.08, -24.44) * mm, "mid": v(-8.55, -24.9) * mm, "end": v(-9.06, -25.3) * mm});
            skArc(sketch, "E56.13.4", {"start": v(-9.51, -25.38) * mm, "mid": v(-9.28, -25.4) * mm, "end": v(-9.06, -25.3) * mm});
            skLineSegment(sketch, "E56.13.5", {"start": v(-9.51, -25.38) * mm, "end": v(-9.72, -25.31) * mm});
            skLineSegment(sketch, "E56.13.6", {"start": v(-9.91, -25.23) * mm, "end": v(-9.72, -25.31) * mm});
            skArc(sketch, "E56.13.7", {"start": v(-10.2, -24.87) * mm, "mid": v(-10.1, -25.08) * mm, "end": v(-9.91, -25.23) * mm});
            skArc(sketch, "E56.13.8", {"start": v(-10.34, -23.57) * mm, "mid": v(-10.3, -24.22) * mm, "end": v(-10.2, -24.87) * mm});
            skArc(sketch, "E56.13.9", {"start": v(-10.2, -22.91) * mm, "mid": v(-10.31, -23.23) * mm, "end": v(-10.34, -23.57) * mm});
            skLineSegment(sketch, "E56.13.10", {"start": v(-10.2, -22.91) * mm, "end": v(-9.97, -22.37) * mm});
            skArc(sketch, "E56.13.11", {"start": v(-9.97, -22.37) * mm, "mid": v(-9.94, -21.77) * mm, "end": v(-10.34, -21.33) * mm});
            skArc(sketch, "E56.14.0", {"start": v(-1.7, -23.65) * mm, "mid": v(-2.27, -23.83) * mm, "end": v(-2.55, -24.35) * mm});
            skLineSegment(sketch, "E56.14.1", {"start": v(-2.62, -24.95) * mm, "end": v(-2.55, -24.35) * mm});
            skArc(sketch, "E56.14.2", {"start": v(-2.82, -25.58) * mm, "mid": v(-2.69, -25.28) * mm, "end": v(-2.62, -24.95) * mm});
            skArc(sketch, "E56.14.3", {"start": v(-2.82, -25.58) * mm, "mid": v(-3.18, -26.13) * mm, "end": v(-3.6, -26.64) * mm});
            skArc(sketch, "E56.14.4", {"start": v(-4.03, -26.8) * mm, "mid": v(-3.8, -26.77) * mm, "end": v(-3.6, -26.64) * mm});
            skLineSegment(sketch, "E56.14.5", {"start": v(-4.03, -26.8) * mm, "end": v(-4.24, -26.78) * mm});
            skLineSegment(sketch, "E56.14.6", {"start": v(-4.45, -26.74) * mm, "end": v(-4.24, -26.78) * mm});
            skArc(sketch, "E56.14.7", {"start": v(-4.8, -26.45) * mm, "mid": v(-4.66, -26.63) * mm, "end": v(-4.45, -26.74) * mm});
            skArc(sketch, "E56.14.8", {"start": v(-5.22, -25.2) * mm, "mid": v(-5.05, -25.84) * mm, "end": v(-4.8, -26.45) * mm});
            skArc(sketch, "E56.14.9", {"start": v(-5.22, -24.53) * mm, "mid": v(-5.26, -24.87) * mm, "end": v(-5.22, -25.2) * mm});
            skLineSegment(sketch, "E56.14.10", {"start": v(-5.22, -24.53) * mm, "end": v(-5.1, -23.95) * mm});
            skArc(sketch, "E56.14.11", {"start": v(-5.1, -23.95) * mm, "mid": v(-5.2, -23.36) * mm, "end": v(-5.68, -23.02) * mm});
            skArc(sketch, "E56.15.0", {"start": v(3.25, -23.48) * mm, "mid": v(2.73, -23.78) * mm, "end": v(2.57, -24.35) * mm});
            skLineSegment(sketch, "E56.15.1", {"start": v(2.63, -24.95) * mm, "end": v(2.57, -24.35) * mm});
            skArc(sketch, "E56.15.2", {"start": v(2.56, -25.61) * mm, "mid": v(2.63, -25.28) * mm, "end": v(2.63, -24.95) * mm});
            skArc(sketch, "E56.15.3", {"start": v(2.56, -25.61) * mm, "mid": v(2.32, -26.22) * mm, "end": v(2.02, -26.8) * mm});
            skArc(sketch, "E56.15.4", {"start": v(1.63, -27.05) * mm, "mid": v(1.86, -26.98) * mm, "end": v(2.02, -26.8) * mm});
            skLineSegment(sketch, "E56.15.5", {"start": v(1.63, -27.05) * mm, "end": v(1.42, -27.08) * mm});
            skLineSegment(sketch, "E56.15.6", {"start": v(1.2, -27.08) * mm, "end": v(1.42, -27.08) * mm});
            skArc(sketch, "E56.15.7", {"start": v(0.8, -26.87) * mm, "mid": v(0.97, -27.02) * mm, "end": v(1.2, -27.08) * mm});
            skArc(sketch, "E56.15.8", {"start": v(0.14, -25.74) * mm, "mid": v(0.44, -26.32) * mm, "end": v(0.8, -26.87) * mm});
            skArc(sketch, "E56.15.9", {"start": v(0, -25.08) * mm, "mid": v(0.03, -25.42) * mm, "end": v(0.14, -25.74) * mm});
            skLineSegment(sketch, "E56.15.10", {"start": v(0, -25.08) * mm, "end": v(0, -24.49) * mm});
            skArc(sketch, "E56.15.11", {"start": v(0, -24.49) * mm, "mid": v(-0.23, -23.94) * mm, "end": v(-0.77, -23.7) * mm});
            skArc(sketch, "E56.16.0", {"start": v(8.06, -22.3) * mm, "mid": v(7.61, -22.7) * mm, "end": v(7.57, -23.29) * mm});
            skLineSegment(sketch, "E56.16.1", {"start": v(7.76, -23.85) * mm, "end": v(7.57, -23.29) * mm});
            skArc(sketch, "E56.16.2", {"start": v(7.82, -24.52) * mm, "mid": v(7.83, -24.18) * mm, "end": v(7.76, -23.85) * mm});
            skArc(sketch, "E56.16.3", {"start": v(7.82, -24.52) * mm, "mid": v(7.72, -25.17) * mm, "end": v(7.55, -25.8) * mm});
            skArc(sketch, "E56.16.4", {"start": v(7.22, -26.12) * mm, "mid": v(7.42, -26) * mm, "end": v(7.55, -25.8) * mm});
            skLineSegment(sketch, "E56.16.5", {"start": v(7.22, -26.12) * mm, "end": v(7.02, -26.19) * mm});
            skLineSegment(sketch, "E56.16.6", {"start": v(6.8, -26.23) * mm, "end": v(7.02, -26.19) * mm});
            skArc(sketch, "E56.16.7", {"start": v(6.36, -26.12) * mm, "mid": v(6.57, -26.23) * mm, "end": v(6.8, -26.23) * mm});
            skArc(sketch, "E56.16.8", {"start": v(5.48, -25.15) * mm, "mid": v(5.9, -25.65) * mm, "end": v(6.36, -26.12) * mm});
            skArc(sketch, "E56.16.9", {"start": v(5.2, -24.54) * mm, "mid": v(5.31, -24.86) * mm, "end": v(5.48, -25.15) * mm});
            skLineSegment(sketch, "E56.16.10", {"start": v(5.2, -24.54) * mm, "end": v(5.09, -23.95) * mm});
            skArc(sketch, "E56.16.11", {"start": v(5.09, -23.95) * mm, "mid": v(4.75, -23.46) * mm, "end": v(4.17, -23.34) * mm});
            skArc(sketch, "E56.17.0", {"start": v(12.52, -20.13) * mm, "mid": v(12.17, -20.61) * mm, "end": v(12.25, -21.2) * mm});
            skLineSegment(sketch, "E56.17.1", {"start": v(12.55, -21.72) * mm, "end": v(12.25, -21.2) * mm});
            skArc(sketch, "E56.17.2", {"start": v(12.75, -22.36) * mm, "mid": v(12.68, -22.03) * mm, "end": v(12.55, -21.72) * mm});
            skArc(sketch, "E56.17.3", {"start": v(12.75, -22.36) * mm, "mid": v(12.78, -23.01) * mm, "end": v(12.75, -23.67) * mm});
            skArc(sketch, "E56.17.4", {"start": v(12.5, -24.05) * mm, "mid": v(12.67, -23.89) * mm, "end": v(12.75, -23.67) * mm});
            skLineSegment(sketch, "E56.17.5", {"start": v(12.5, -24.05) * mm, "end": v(12.3, -24.16) * mm});
            skLineSegment(sketch, "E56.17.6", {"start": v(12.11, -24.25) * mm, "end": v(12.3, -24.16) * mm});
            skArc(sketch, "E56.17.7", {"start": v(11.65, -24.22) * mm, "mid": v(11.88, -24.29) * mm, "end": v(12.11, -24.25) * mm});
            skArc(sketch, "E56.17.8", {"start": v(10.6, -23.46) * mm, "mid": v(11.1, -23.87) * mm, "end": v(11.65, -24.22) * mm});
            skArc(sketch, "E56.17.9", {"start": v(10.2, -22.92) * mm, "mid": v(10.37, -23.2) * mm, "end": v(10.6, -23.46) * mm});
            skLineSegment(sketch, "E56.17.10", {"start": v(10.2, -22.92) * mm, "end": v(9.95, -22.37) * mm});
            skArc(sketch, "E56.17.11", {"start": v(9.95, -22.37) * mm, "mid": v(9.53, -21.96) * mm, "end": v(8.93, -21.96) * mm});
            skArc(sketch, "E56.18.0", {"start": v(16.43, -17.1) * mm, "mid": v(16.19, -17.63) * mm, "end": v(16.39, -18.2) * mm});
            skLineSegment(sketch, "E56.18.1", {"start": v(16.79, -18.64) * mm, "end": v(16.39, -18.2) * mm});
            skArc(sketch, "E56.18.2", {"start": v(17.12, -19.22) * mm, "mid": v(16.99, -18.9) * mm, "end": v(16.79, -18.64) * mm});
            skArc(sketch, "E56.18.3", {"start": v(17.12, -19.22) * mm, "mid": v(17.29, -19.85) * mm, "end": v(17.39, -20.5) * mm});
            skArc(sketch, "E56.18.4", {"start": v(17.22, -20.93) * mm, "mid": v(17.36, -20.73) * mm, "end": v(17.39, -20.5) * mm});
            skLineSegment(sketch, "E56.18.5", {"start": v(17.22, -20.93) * mm, "end": v(17.06, -21.07) * mm});
            skLineSegment(sketch, "E56.18.6", {"start": v(16.89, -21.2) * mm, "end": v(17.06, -21.07) * mm});
            skArc(sketch, "E56.18.7", {"start": v(16.44, -21.27) * mm, "mid": v(16.67, -21.29) * mm, "end": v(16.89, -21.2) * mm});
            skArc(sketch, "E56.18.8", {"start": v(15.24, -20.74) * mm, "mid": v(15.82, -21.04) * mm, "end": v(16.44, -21.27) * mm});
            skArc(sketch, "E56.18.9", {"start": v(14.74, -20.3) * mm, "mid": v(14.96, -20.55) * mm, "end": v(15.24, -20.74) * mm});
            skLineSegment(sketch, "E56.18.10", {"start": v(14.74, -20.3) * mm, "end": v(14.39, -19.81) * mm});
            skArc(sketch, "E56.18.11", {"start": v(14.39, -19.81) * mm, "mid": v(13.88, -19.5) * mm, "end": v(13.3, -19.62) * mm});
            skArc(sketch, "E56.19.0", {"start": v(19.62, -13.3) * mm, "mid": v(19.5, -13.88) * mm, "end": v(19.81, -14.39) * mm});
            skLineSegment(sketch, "E56.19.1", {"start": v(20.3, -14.74) * mm, "end": v(19.81, -14.39) * mm});
            skArc(sketch, "E56.19.2", {"start": v(20.74, -15.24) * mm, "mid": v(20.55, -14.96) * mm, "end": v(20.3, -14.74) * mm});
            skArc(sketch, "E56.19.3", {"start": v(20.74, -15.24) * mm, "mid": v(21.04, -15.82) * mm, "end": v(21.27, -16.44) * mm});
            skArc(sketch, "E56.19.4", {"start": v(21.2, -16.89) * mm, "mid": v(21.29, -16.67) * mm, "end": v(21.27, -16.44) * mm});
            skLineSegment(sketch, "E56.19.5", {"start": v(21.2, -16.89) * mm, "end": v(21.07, -17.06) * mm});
            skLineSegment(sketch, "E56.19.6", {"start": v(20.93, -17.22) * mm, "end": v(21.07, -17.06) * mm});
            skArc(sketch, "E56.19.7", {"start": v(20.5, -17.39) * mm, "mid": v(20.73, -17.36) * mm, "end": v(20.93, -17.22) * mm});
            skArc(sketch, "E56.19.8", {"start": v(19.22, -17.12) * mm, "mid": v(19.85, -17.29) * mm, "end": v(20.5, -17.39) * mm});
            skArc(sketch, "E56.19.9", {"start": v(18.64, -16.79) * mm, "mid": v(18.9, -16.99) * mm, "end": v(19.22, -17.12) * mm});
            skLineSegment(sketch, "E56.19.10", {"start": v(18.64, -16.79) * mm, "end": v(18.2, -16.39) * mm});
            skArc(sketch, "E56.19.11", {"start": v(18.2, -16.39) * mm, "mid": v(17.63, -16.19) * mm, "end": v(17.1, -16.43) * mm});
            skArc(sketch, "E56.20.0", {"start": v(21.96, -8.93) * mm, "mid": v(21.96, -9.53) * mm, "end": v(22.37, -9.95) * mm});
            skLineSegment(sketch, "E56.20.1", {"start": v(22.92, -10.2) * mm, "end": v(22.37, -9.95) * mm});
            skArc(sketch, "E56.20.2", {"start": v(23.46, -10.6) * mm, "mid": v(23.2, -10.37) * mm, "end": v(22.92, -10.2) * mm});
            skArc(sketch, "E56.20.3", {"start": v(23.46, -10.6) * mm, "mid": v(23.87, -11.1) * mm, "end": v(24.22, -11.65) * mm});
            skArc(sketch, "E56.20.4", {"start": v(24.25, -12.11) * mm, "mid": v(24.29, -11.88) * mm, "end": v(24.22, -11.65) * mm});
            skLineSegment(sketch, "E56.20.5", {"start": v(24.25, -12.11) * mm, "end": v(24.16, -12.3) * mm});
            skLineSegment(sketch, "E56.20.6", {"start": v(24.05, -12.5) * mm, "end": v(24.16, -12.3) * mm});
            skArc(sketch, "E56.20.7", {"start": v(23.67, -12.75) * mm, "mid": v(23.89, -12.67) * mm, "end": v(24.05, -12.5) * mm});
            skArc(sketch, "E56.20.8", {"start": v(22.36, -12.75) * mm, "mid": v(23.01, -12.78) * mm, "end": v(23.67, -12.75) * mm});
            skArc(sketch, "E56.20.9", {"start": v(21.72, -12.55) * mm, "mid": v(22.03, -12.68) * mm, "end": v(22.36, -12.75) * mm});
            skLineSegment(sketch, "E56.20.10", {"start": v(21.72, -12.55) * mm, "end": v(21.2, -12.25) * mm});
            skArc(sketch, "E56.20.11", {"start": v(21.2, -12.25) * mm, "mid": v(20.61, -12.17) * mm, "end": v(20.13, -12.52) * mm});
            skArc(sketch, "E56.21.0", {"start": v(23.34, -4.17) * mm, "mid": v(23.46, -4.75) * mm, "end": v(23.95, -5.09) * mm});
            skLineSegment(sketch, "E56.21.1", {"start": v(24.54, -5.2) * mm, "end": v(23.95, -5.09) * mm});
            skArc(sketch, "E56.21.2", {"start": v(25.15, -5.48) * mm, "mid": v(24.86, -5.31) * mm, "end": v(24.54, -5.2) * mm});
            skArc(sketch, "E56.21.3", {"start": v(25.15, -5.48) * mm, "mid": v(25.65, -5.9) * mm, "end": v(26.12, -6.36) * mm});
            skArc(sketch, "E56.21.4", {"start": v(26.23, -6.8) * mm, "mid": v(26.23, -6.57) * mm, "end": v(26.12, -6.36) * mm});
            skLineSegment(sketch, "E56.21.5", {"start": v(26.23, -6.8) * mm, "end": v(26.19, -7.02) * mm});
            skLineSegment(sketch, "E56.21.6", {"start": v(26.12, -7.22) * mm, "end": v(26.19, -7.02) * mm});
            skArc(sketch, "E56.21.7", {"start": v(25.8, -7.55) * mm, "mid": v(26, -7.42) * mm, "end": v(26.12, -7.22) * mm});
            skArc(sketch, "E56.21.8", {"start": v(24.52, -7.82) * mm, "mid": v(25.17, -7.72) * mm, "end": v(25.8, -7.55) * mm});
            skArc(sketch, "E56.21.9", {"start": v(23.85, -7.76) * mm, "mid": v(24.18, -7.83) * mm, "end": v(24.52, -7.82) * mm});
            skLineSegment(sketch, "E56.21.10", {"start": v(23.85, -7.76) * mm, "end": v(23.29, -7.57) * mm});
            skArc(sketch, "E56.21.11", {"start": v(23.29, -7.57) * mm, "mid": v(22.7, -7.61) * mm, "end": v(22.3, -8.06) * mm});
            skArc(sketch, "E56.22.0", {"start": v(23.7, 0.77) * mm, "mid": v(23.94, 0.23) * mm, "end": v(24.49, 0) * mm});
            skLineSegment(sketch, "E56.22.1", {"start": v(25.08, 0) * mm, "end": v(24.49, 0) * mm});
            skArc(sketch, "E56.22.2", {"start": v(25.74, -0.14) * mm, "mid": v(25.42, -0.03) * mm, "end": v(25.08, 0) * mm});
            skArc(sketch, "E56.22.3", {"start": v(25.74, -0.14) * mm, "mid": v(26.32, -0.44) * mm, "end": v(26.87, -0.8) * mm});
            skArc(sketch, "E56.22.4", {"start": v(27.08, -1.2) * mm, "mid": v(27.02, -0.97) * mm, "end": v(26.87, -0.8) * mm});
            skLineSegment(sketch, "E56.22.5", {"start": v(27.08, -1.2) * mm, "end": v(27.08, -1.42) * mm});
            skLineSegment(sketch, "E56.22.6", {"start": v(27.05, -1.63) * mm, "end": v(27.08, -1.42) * mm});
            skArc(sketch, "E56.22.7", {"start": v(26.8, -2.02) * mm, "mid": v(26.98, -1.86) * mm, "end": v(27.05, -1.63) * mm});
            skArc(sketch, "E56.22.8", {"start": v(25.61, -2.56) * mm, "mid": v(26.22, -2.32) * mm, "end": v(26.8, -2.02) * mm});
            skArc(sketch, "E56.22.9", {"start": v(24.95, -2.63) * mm, "mid": v(25.28, -2.63) * mm, "end": v(25.61, -2.56) * mm});
            skLineSegment(sketch, "E56.22.10", {"start": v(24.95, -2.63) * mm, "end": v(24.35, -2.57) * mm});
            skArc(sketch, "E56.22.11", {"start": v(24.35, -2.57) * mm, "mid": v(23.78, -2.73) * mm, "end": v(23.48, -3.25) * mm});
            skArc(sketch, "E56.23.0", {"start": v(23.02, 5.68) * mm, "mid": v(23.36, 5.2) * mm, "end": v(23.95, 5.1) * mm});
            skLineSegment(sketch, "E56.23.1", {"start": v(24.53, 5.22) * mm, "end": v(23.95, 5.1) * mm});
            skArc(sketch, "E56.23.2", {"start": v(25.2, 5.22) * mm, "mid": v(24.87, 5.26) * mm, "end": v(24.53, 5.22) * mm});
            skArc(sketch, "E56.23.3", {"start": v(25.2, 5.22) * mm, "mid": v(25.84, 5.05) * mm, "end": v(26.45, 4.8) * mm});
            skArc(sketch, "E56.23.4", {"start": v(26.74, 4.45) * mm, "mid": v(26.63, 4.66) * mm, "end": v(26.45, 4.8) * mm});
            skLineSegment(sketch, "E56.23.5", {"start": v(26.74, 4.45) * mm, "end": v(26.78, 4.24) * mm});
            skLineSegment(sketch, "E56.23.6", {"start": v(26.8, 4.03) * mm, "end": v(26.78, 4.24) * mm});
            skArc(sketch, "E56.23.7", {"start": v(26.64, 3.6) * mm, "mid": v(26.77, 3.8) * mm, "end": v(26.8, 4.03) * mm});
            skArc(sketch, "E56.23.8", {"start": v(25.58, 2.82) * mm, "mid": v(26.13, 3.18) * mm, "end": v(26.64, 3.6) * mm});
            skArc(sketch, "E56.23.9", {"start": v(24.95, 2.62) * mm, "mid": v(25.28, 2.69) * mm, "end": v(25.58, 2.82) * mm});
            skLineSegment(sketch, "E56.23.10", {"start": v(24.95, 2.62) * mm, "end": v(24.35, 2.55) * mm});
            skArc(sketch, "E56.23.11", {"start": v(24.35, 2.55) * mm, "mid": v(23.83, 2.27) * mm, "end": v(23.65, 1.7) * mm});
            skArc(sketch, "E56.24.0", {"start": v(21.33, 10.34) * mm, "mid": v(21.77, 9.94) * mm, "end": v(22.37, 9.97) * mm});
            skLineSegment(sketch, "E56.24.1", {"start": v(22.91, 10.2) * mm, "end": v(22.37, 9.97) * mm});
            skArc(sketch, "E56.24.2", {"start": v(23.57, 10.34) * mm, "mid": v(23.23, 10.31) * mm, "end": v(22.91, 10.2) * mm});
            skArc(sketch, "E56.24.3", {"start": v(23.57, 10.34) * mm, "mid": v(24.22, 10.3) * mm, "end": v(24.87, 10.2) * mm});
            skArc(sketch, "E56.24.4", {"start": v(25.23, 9.91) * mm, "mid": v(25.08, 10.1) * mm, "end": v(24.87, 10.2) * mm});
            skLineSegment(sketch, "E56.24.5", {"start": v(25.23, 9.91) * mm, "end": v(25.31, 9.72) * mm});
            skLineSegment(sketch, "E56.24.6", {"start": v(25.38, 9.51) * mm, "end": v(25.31, 9.72) * mm});
            skArc(sketch, "E56.24.7", {"start": v(25.3, 9.06) * mm, "mid": v(25.4, 9.28) * mm, "end": v(25.38, 9.51) * mm});
            skArc(sketch, "E56.24.8", {"start": v(24.44, 8.08) * mm, "mid": v(24.9, 8.55) * mm, "end": v(25.3, 9.06) * mm});
            skArc(sketch, "E56.24.9", {"start": v(23.86, 7.75) * mm, "mid": v(24.16, 7.88) * mm, "end": v(24.44, 8.08) * mm});
            skLineSegment(sketch, "E56.24.10", {"start": v(23.86, 7.75) * mm, "end": v(23.3, 7.56) * mm});
            skArc(sketch, "E56.24.11", {"start": v(23.3, 7.56) * mm, "mid": v(22.83, 7.18) * mm, "end": v(22.77, 6.59) * mm});
            skArc(sketch, "E56.25.0", {"start": v(18.71, 14.55) * mm, "mid": v(19.23, 14.25) * mm, "end": v(19.8, 14.4) * mm});
            skLineSegment(sketch, "E56.25.1", {"start": v(20.29, 14.75) * mm, "end": v(19.8, 14.4) * mm});
            skArc(sketch, "E56.25.2", {"start": v(20.9, 15.02) * mm, "mid": v(20.58, 14.92) * mm, "end": v(20.29, 14.75) * mm});
            skArc(sketch, "E56.25.3", {"start": v(20.9, 15.02) * mm, "mid": v(21.55, 15.12) * mm, "end": v(22.2, 15.15) * mm});
            skArc(sketch, "E56.25.4", {"start": v(22.61, 14.94) * mm, "mid": v(22.43, 15.1) * mm, "end": v(22.2, 15.15) * mm});
            skLineSegment(sketch, "E56.25.5", {"start": v(22.61, 14.94) * mm, "end": v(22.74, 14.77) * mm});
            skLineSegment(sketch, "E56.25.6", {"start": v(22.85, 14.58) * mm, "end": v(22.74, 14.77) * mm});
            skArc(sketch, "E56.25.7", {"start": v(22.87, 14.12) * mm, "mid": v(22.91, 14.35) * mm, "end": v(22.85, 14.58) * mm});
            skArc(sketch, "E56.25.8", {"start": v(22.22, 12.99) * mm, "mid": v(22.58, 13.54) * mm, "end": v(22.87, 14.12) * mm});
            skArc(sketch, "E56.25.9", {"start": v(21.73, 12.54) * mm, "mid": v(22, 12.73) * mm, "end": v(22.22, 12.99) * mm});
            skLineSegment(sketch, "E56.25.10", {"start": v(21.73, 12.54) * mm, "end": v(21.2, 12.24) * mm});
            skArc(sketch, "E56.25.11", {"start": v(21.2, 12.24) * mm, "mid": v(20.84, 11.77) * mm, "end": v(20.9, 11.18) * mm});
            skArc(sketch, "E56.26.0", {"start": v(15.28, 18.13) * mm, "mid": v(15.85, 17.94) * mm, "end": v(16.38, 18.2) * mm});
            skLineSegment(sketch, "E56.26.1", {"start": v(16.78, 18.64) * mm, "end": v(16.38, 18.2) * mm});
            skArc(sketch, "E56.26.2", {"start": v(17.32, 19.04) * mm, "mid": v(17.03, 18.87) * mm, "end": v(16.78, 18.64) * mm});
            skArc(sketch, "E56.26.3", {"start": v(17.32, 19.04) * mm, "mid": v(17.94, 19.27) * mm, "end": v(18.57, 19.44) * mm});
            skArc(sketch, "E56.26.4", {"start": v(19.01, 19.32) * mm, "mid": v(18.8, 19.43) * mm, "end": v(18.57, 19.44) * mm});
            skLineSegment(sketch, "E56.26.5", {"start": v(19.01, 19.32) * mm, "end": v(19.17, 19.17) * mm});
            skLineSegment(sketch, "E56.26.6", {"start": v(19.32, 19.01) * mm, "end": v(19.17, 19.17) * mm});
            skArc(sketch, "E56.26.7", {"start": v(19.44, 18.57) * mm, "mid": v(19.43, 18.8) * mm, "end": v(19.32, 19.01) * mm});
            skArc(sketch, "E56.26.8", {"start": v(19.04, 17.32) * mm, "mid": v(19.27, 17.94) * mm, "end": v(19.44, 18.57) * mm});
            skArc(sketch, "E56.26.9", {"start": v(18.64, 16.78) * mm, "mid": v(18.87, 17.03) * mm, "end": v(19.04, 17.32) * mm});
            skLineSegment(sketch, "E56.26.10", {"start": v(18.64, 16.78) * mm, "end": v(18.2, 16.38) * mm});
            skArc(sketch, "E56.26.11", {"start": v(18.2, 16.38) * mm, "mid": v(17.94, 15.85) * mm, "end": v(18.13, 15.28) * mm});
            skArc(sketch, "E56.27.0", {"start": v(11.18, 20.9) * mm, "mid": v(11.77, 20.84) * mm, "end": v(12.24, 21.2) * mm});
            skLineSegment(sketch, "E56.27.1", {"start": v(12.54, 21.73) * mm, "end": v(12.24, 21.2) * mm});
            skArc(sketch, "E56.27.2", {"start": v(12.99, 22.22) * mm, "mid": v(12.73, 22) * mm, "end": v(12.54, 21.73) * mm});
            skArc(sketch, "E56.27.3", {"start": v(12.99, 22.22) * mm, "mid": v(13.54, 22.58) * mm, "end": v(14.12, 22.87) * mm});
            skArc(sketch, "E56.27.4", {"start": v(14.58, 22.85) * mm, "mid": v(14.35, 22.91) * mm, "end": v(14.12, 22.87) * mm});
            skLineSegment(sketch, "E56.27.5", {"start": v(14.58, 22.85) * mm, "end": v(14.77, 22.74) * mm});
            skLineSegment(sketch, "E56.27.6", {"start": v(14.94, 22.61) * mm, "end": v(14.77, 22.74) * mm});
            skArc(sketch, "E56.27.7", {"start": v(15.15, 22.2) * mm, "mid": v(15.1, 22.43) * mm, "end": v(14.94, 22.61) * mm});
            skArc(sketch, "E56.27.8", {"start": v(15.02, 20.9) * mm, "mid": v(15.12, 21.55) * mm, "end": v(15.15, 22.2) * mm});
            skArc(sketch, "E56.27.9", {"start": v(14.75, 20.29) * mm, "mid": v(14.92, 20.58) * mm, "end": v(15.02, 20.9) * mm});
            skLineSegment(sketch, "E56.27.10", {"start": v(14.75, 20.29) * mm, "end": v(14.4, 19.8) * mm});
            skArc(sketch, "E56.27.11", {"start": v(14.4, 19.8) * mm, "mid": v(14.25, 19.23) * mm, "end": v(14.55, 18.71) * mm});
            skArc(sketch, "E56.28.0", {"start": v(6.59, 22.77) * mm, "mid": v(7.18, 22.83) * mm, "end": v(7.56, 23.3) * mm});
            skLineSegment(sketch, "E56.28.1", {"start": v(7.75, 23.86) * mm, "end": v(7.56, 23.3) * mm});
            skArc(sketch, "E56.28.2", {"start": v(8.08, 24.44) * mm, "mid": v(7.88, 24.16) * mm, "end": v(7.75, 23.86) * mm});
            skArc(sketch, "E56.28.3", {"start": v(8.08, 24.44) * mm, "mid": v(8.55, 24.9) * mm, "end": v(9.06, 25.3) * mm});
            skArc(sketch, "E56.28.4", {"start": v(9.51, 25.38) * mm, "mid": v(9.28, 25.4) * mm, "end": v(9.06, 25.3) * mm});
            skLineSegment(sketch, "E56.28.5", {"start": v(9.51, 25.38) * mm, "end": v(9.72, 25.31) * mm});
            skLineSegment(sketch, "E56.28.6", {"start": v(9.91, 25.23) * mm, "end": v(9.72, 25.31) * mm});
            skArc(sketch, "E56.28.7", {"start": v(10.2, 24.87) * mm, "mid": v(10.1, 25.08) * mm, "end": v(9.91, 25.23) * mm});
            skArc(sketch, "E56.28.8", {"start": v(10.34, 23.57) * mm, "mid": v(10.3, 24.22) * mm, "end": v(10.2, 24.87) * mm});
            skArc(sketch, "E56.28.9", {"start": v(10.2, 22.91) * mm, "mid": v(10.31, 23.23) * mm, "end": v(10.34, 23.57) * mm});
            skLineSegment(sketch, "E56.28.10", {"start": v(10.2, 22.91) * mm, "end": v(9.97, 22.37) * mm});
            skArc(sketch, "E56.28.11", {"start": v(9.97, 22.37) * mm, "mid": v(9.94, 21.77) * mm, "end": v(10.34, 21.33) * mm});
            skArc(sketch, "E56.29.0", {"start": v(1.7, 23.65) * mm, "mid": v(2.27, 23.83) * mm, "end": v(2.55, 24.35) * mm});
            skLineSegment(sketch, "E56.29.1", {"start": v(2.62, 24.95) * mm, "end": v(2.55, 24.35) * mm});
            skArc(sketch, "E56.29.2", {"start": v(2.82, 25.58) * mm, "mid": v(2.69, 25.28) * mm, "end": v(2.62, 24.95) * mm});
            skArc(sketch, "E56.29.3", {"start": v(2.82, 25.58) * mm, "mid": v(3.18, 26.13) * mm, "end": v(3.6, 26.64) * mm});
            skArc(sketch, "E56.29.4", {"start": v(4.03, 26.8) * mm, "mid": v(3.8, 26.77) * mm, "end": v(3.6, 26.64) * mm});
            skLineSegment(sketch, "E56.29.5", {"start": v(4.03, 26.8) * mm, "end": v(4.24, 26.78) * mm});
            skLineSegment(sketch, "E56.29.6", {"start": v(4.45, 26.74) * mm, "end": v(4.24, 26.78) * mm});
            skArc(sketch, "E56.29.7", {"start": v(4.8, 26.45) * mm, "mid": v(4.66, 26.63) * mm, "end": v(4.45, 26.74) * mm});
            skArc(sketch, "E56.29.8", {"start": v(5.22, 25.2) * mm, "mid": v(5.05, 25.84) * mm, "end": v(4.8, 26.45) * mm});
            skArc(sketch, "E56.29.9", {"start": v(5.22, 24.53) * mm, "mid": v(5.26, 24.87) * mm, "end": v(5.22, 25.2) * mm});
            skLineSegment(sketch, "E56.29.10", {"start": v(5.22, 24.53) * mm, "end": v(5.1, 23.95) * mm});
            skArc(sketch, "E56.29.11", {"start": v(5.1, 23.95) * mm, "mid": v(5.2, 23.36) * mm, "end": v(5.68, 23.02) * mm});
            skArc(sketch, "E57.trimOffspring", {"start": v(1.7, 23.65) * mm, "mid": v(1.24, 23.67) * mm, "end": v(0.77, 23.7) * mm});
            skArc(sketch, "E58.trimOffspring", {"start": v(6.59, 22.77) * mm, "mid": v(6.14, 22.9) * mm, "end": v(5.68, 23.02) * mm});
            skArc(sketch, "E59.trimOffspring", {"start": v(11.18, 20.9) * mm, "mid": v(10.76, 21.12) * mm, "end": v(10.34, 21.33) * mm});
            skArc(sketch, "E60.trimOffspring", {"start": v(15.28, 18.13) * mm, "mid": v(14.92, 18.42) * mm, "end": v(14.55, 18.71) * mm});
            skArc(sketch, "E61.trimOffspring", {"start": v(18.71, 14.55) * mm, "mid": v(18.42, 14.92) * mm, "end": v(18.13, 15.28) * mm});
            skArc(sketch, "E62.trimOffspring", {"start": v(21.33, 10.34) * mm, "mid": v(21.12, 10.76) * mm, "end": v(20.9, 11.18) * mm});
            skArc(sketch, "E63.trimOffspring", {"start": v(23.02, 5.68) * mm, "mid": v(22.9, 6.14) * mm, "end": v(22.77, 6.59) * mm});
            skArc(sketch, "E64.trimOffspring", {"start": v(23.7, 0.77) * mm, "mid": v(23.67, 1.24) * mm, "end": v(23.65, 1.7) * mm});
            skArc(sketch, "E65.trimOffspring", {"start": v(23.34, -4.17) * mm, "mid": v(23.41, -3.7) * mm, "end": v(23.48, -3.25) * mm});
            skArc(sketch, "E66.trimOffspring", {"start": v(21.96, -8.93) * mm, "mid": v(22.13, -8.5) * mm, "end": v(22.3, -8.06) * mm});
            skArc(sketch, "E67.trimOffspring", {"start": v(19.62, -13.3) * mm, "mid": v(19.88, -12.91) * mm, "end": v(20.13, -12.52) * mm});
            skArc(sketch, "E68.trimOffspring", {"start": v(16.43, -17.1) * mm, "mid": v(16.76, -16.76) * mm, "end": v(17.1, -16.43) * mm});
            skArc(sketch, "E69.trimOffspring", {"start": v(12.52, -20.13) * mm, "mid": v(12.91, -19.88) * mm, "end": v(13.3, -19.62) * mm});
            skArc(sketch, "E70.trimOffspring", {"start": v(8.06, -22.3) * mm, "mid": v(8.5, -22.13) * mm, "end": v(8.93, -21.96) * mm});
            skArc(sketch, "E71.trimOffspring", {"start": v(3.25, -23.48) * mm, "mid": v(3.7, -23.41) * mm, "end": v(4.17, -23.34) * mm});
            skArc(sketch, "E72.trimOffspring", {"start": v(-1.7, -23.65) * mm, "mid": v(-1.24, -23.67) * mm, "end": v(-0.77, -23.7) * mm});
            skArc(sketch, "E73.trimOffspring", {"start": v(-6.59, -22.77) * mm, "mid": v(-6.14, -22.9) * mm, "end": v(-5.68, -23.02) * mm});
            skArc(sketch, "E74.trimOffspring", {"start": v(-11.18, -20.9) * mm, "mid": v(-10.76, -21.12) * mm, "end": v(-10.34, -21.33) * mm});
            skArc(sketch, "E75.trimOffspring", {"start": v(-15.28, -18.13) * mm, "mid": v(-14.92, -18.42) * mm, "end": v(-14.55, -18.71) * mm});
            skArc(sketch, "E76.trimOffspring", {"start": v(-18.71, -14.55) * mm, "mid": v(-18.42, -14.92) * mm, "end": v(-18.13, -15.28) * mm});
            skArc(sketch, "E77.trimOffspring", {"start": v(-21.33, -10.34) * mm, "mid": v(-21.12, -10.76) * mm, "end": v(-20.9, -11.18) * mm});
            skArc(sketch, "E78.trimOffspring", {"start": v(-23.02, -5.68) * mm, "mid": v(-22.9, -6.14) * mm, "end": v(-22.77, -6.59) * mm});
            skArc(sketch, "E79.trimOffspring", {"start": v(-8.06, 22.3) * mm, "mid": v(-8.5, 22.13) * mm, "end": v(-8.93, 21.96) * mm});
            skArc(sketch, "E80.trimOffspring", {"start": v(-12.52, 20.13) * mm, "mid": v(-12.91, 19.88) * mm, "end": v(-13.3, 19.62) * mm});
            skArc(sketch, "E81.trimOffspring", {"start": v(-16.43, 17.1) * mm, "mid": v(-16.76, 16.76) * mm, "end": v(-17.1, 16.43) * mm});
            skArc(sketch, "E82.trimOffspring", {"start": v(-23.7, -0.77) * mm, "mid": v(-23.67, -1.24) * mm, "end": v(-23.65, -1.7) * mm});
            skArc(sketch, "E83.trimOffspring", {"start": v(-23.34, 4.17) * mm, "mid": v(-23.41, 3.7) * mm, "end": v(-23.48, 3.25) * mm});
            skArc(sketch, "E84.trimOffspring", {"start": v(-21.96, 8.93) * mm, "mid": v(-22.13, 8.5) * mm, "end": v(-22.3, 8.06) * mm});
            skArc(sketch, "E85.trimOffspring", {"start": v(-19.62, 13.3) * mm, "mid": v(-19.88, 12.91) * mm, "end": v(-20.13, 12.52) * mm});
            skSolve(sketch);
        }
        {
            var Q0;
            Q0=makeQuery(id+"F0.imprint","IMPRINT",FACE,{"disambiguationData":[TD([[makeQuery(id+"F0.imprint","IMPRINT",EDGE,{"derivedFrom":sQuery(id+"F0.wireOp",EDGE,"E0")}),1.0]])]});
            var Q1;
            Q1=makeQuery(id+"F2.imprint","IMPRINT",FACE,{"disambiguationData":[TD([[makeQuery(id+"F2.imprint","IMPRINT",EDGE,{"derivedFrom":sQuery(id+"F2.wireOp",EDGE,"E43")}),1.0]])]});
            var Q2;
            Q2=sQuery(id+"F0.wireOp",VERTEX,"E13.29.3.start");
            var Q3;
            Q3=sQuery(id+"F2.wireOp",VERTEX,"E56.1.3.start");
            loft(context, id + "F3", {"sheetProfilesArray" : [{ "sheetProfileEntities" : qUnion([Q0]) }, { "sheetProfileEntities" : qUnion([Q1]) }], "matchConnections" : true, "connections" : [{ "connectionEntities" : qUnion([Q2, Q3]), "connectionEdgeQueries" : qUnion([]), "connectionEdgeParameters" : [] }]});
        }
        {
            var Q0;
            Q0=makeQuery(id+"F3.opLoft","CAP_FACE",FACE,{"disambiguationData":[OSD([makeQuery(id+"F2.imprint","IMPRINT",FACE,{"disambiguationData":[TD([[makeQuery(id+"F2.imprint","IMPRINT",EDGE,{"derivedFrom":sQuery(id+"F2.wireOp",EDGE,"E43")}),1.0]])]})])],"isStart":true});
            var sketch = newSketch(context, id + "F4", { "sketchPlane" : qUnion([Q0])});
            skPoint(sketch, "E86", {"position": v(0, 0) * mm});
            skSolve(sketch);
        }
        {
            var Q0;
            Q0=sQuery(id+"F4.wireOp",VERTEX,"E86");
            var Q1;
            Q1=makeQuery(id+"F3.opLoft","SWEPT_BODY",BODY,{"disambiguationData":[OSD([makeQuery(id+"F0.imprint","IMPRINT",FACE,{"disambiguationData":[TD([[makeQuery(id+"F0.imprint","IMPRINT",EDGE,{"derivedFrom":sQuery(id+"F0.wireOp",EDGE,"E0")}),1.0]])]}),makeQuery(id+"F2.imprint","IMPRINT",FACE,{"disambiguationData":[TD([[makeQuery(id+"F2.imprint","IMPRINT",EDGE,{"derivedFrom":sQuery(id+"F2.wireOp",EDGE,"E43")}),1.0]])]})])]});
            hole(context, id + "F5", {"style" : HoleStyle.SIMPLE, "endStyle" : HoleEndStyle.THROUGH, "holeDiameter" : 12.7 * mm, "majorDiameter" : 6.35 * mm, "tappedDepth" : 12.7 * mm, "tapClearance" : 3, "locations" : qUnion([Q0]), "scope" : qUnion([Q1])});
        }
    });
